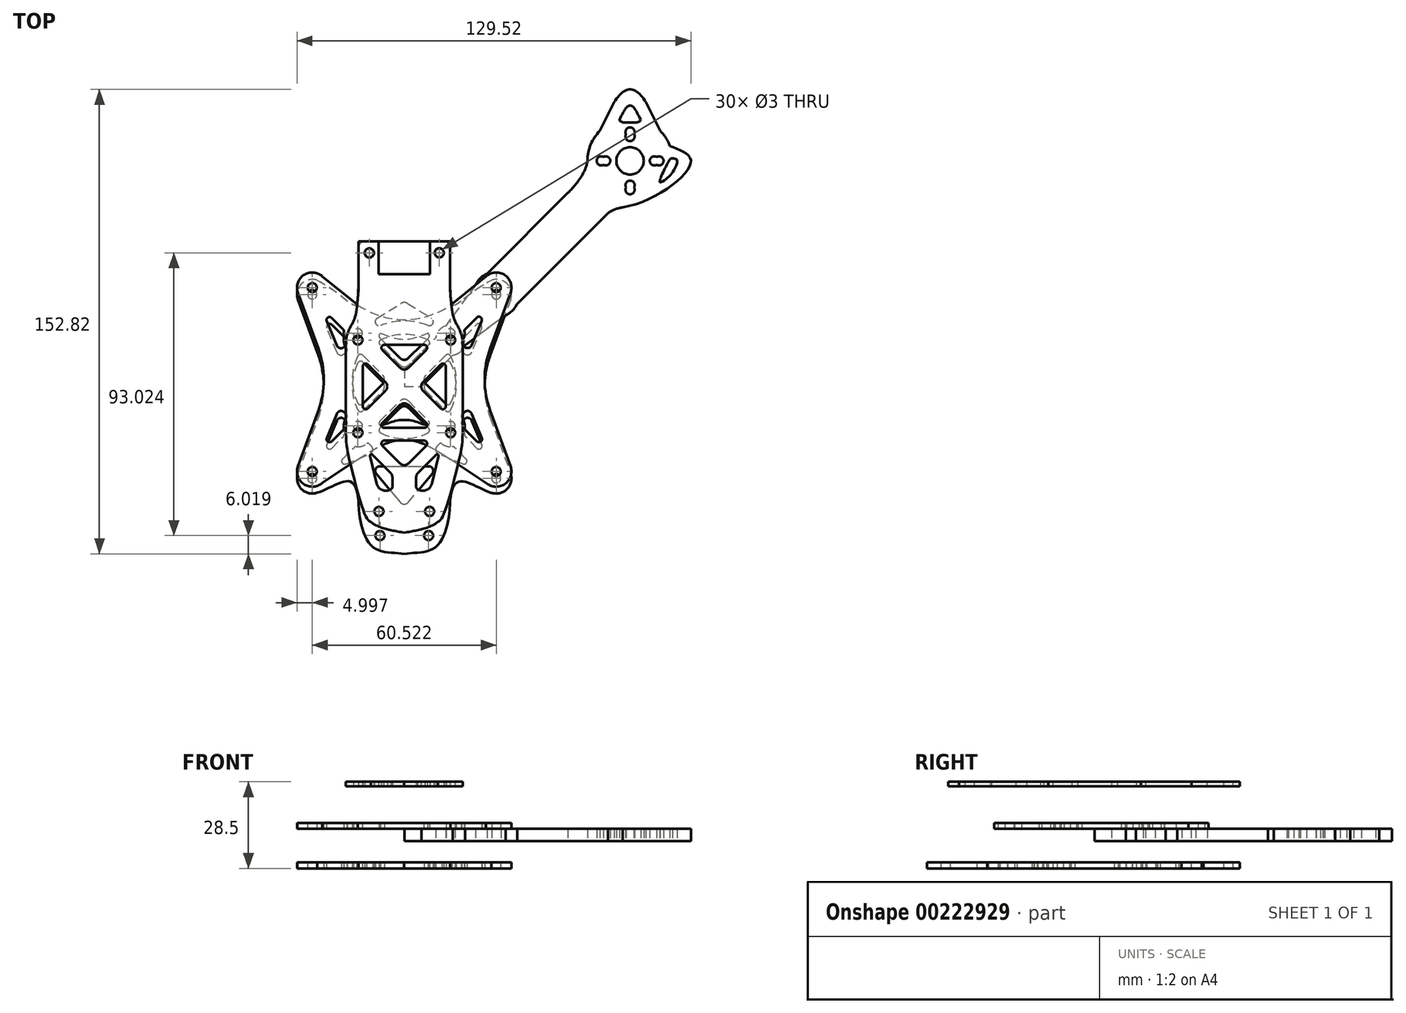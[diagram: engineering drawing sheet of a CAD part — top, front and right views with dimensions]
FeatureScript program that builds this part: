
annotation { "Feature Type Name" : "Feature", "Feature Type Description" : "" }
export const myFeature = defineFeature(function(context is Context, id is Id, definition is map)
    precondition{}
    {
        {
            var Q0;
            Q0=qCreatedBy(makeId("Top.planeOp"),FACE);
            var sketch = newSketch(context, id + "F0", { "sketchPlane" : qUnion([Q0])});
            skLineSegment(sketch, "E0.bottom", {"start": v(-15.25, 15.25) * mm, "end": v(15.25, 15.25) * mm, "construction": true});
            skLineSegment(sketch, "E0.top", {"start": v(-15.25, -15.25) * mm, "end": v(15.25, -15.25) * mm, "construction": true});
            skLineSegment(sketch, "E0.left", {"start": v(-15.25, 15.25) * mm, "end": v(-15.25, -15.25) * mm, "construction": true});
            skLineSegment(sketch, "E0.right", {"start": v(15.25, 15.25) * mm, "end": v(15.25, -15.25) * mm, "construction": true});
            skPoint(sketch, "E0.middle", {"position": v(0, 0) * mm});
            skLineSegment(sketch, "E1.bottom", {"start": v(30.25, 30.25) * mm, "end": v(-30.25, 30.25) * mm, "construction": true});
            skLineSegment(sketch, "E1.top", {"start": v(30.25, -30.25) * mm, "end": v(-30.25, -30.25) * mm, "construction": true});
            skLineSegment(sketch, "E1.left", {"start": v(30.25, 30.25) * mm, "end": v(30.25, -30.25) * mm, "construction": true});
            skLineSegment(sketch, "E1.right", {"start": v(-30.25, 30.25) * mm, "end": v(-30.25, -30.25) * mm, "construction": true});
            skLineSegment(sketch, "E2.bottom", {"start": v(-74.25, 74.24) * mm, "end": v(74.25, 74.24) * mm, "construction": true});
            skLineSegment(sketch, "E2.top", {"start": v(-74.25, -74.25) * mm, "end": v(74.24, -74.25) * mm, "construction": true});
            skLineSegment(sketch, "E2.left", {"start": v(-74.25, 74.24) * mm, "end": v(-74.25, -74.25) * mm, "construction": true});
            skLineSegment(sketch, "E2.right", {"start": v(74.24, 74.24) * mm, "end": v(74.24, -74.25) * mm, "construction": true});
            skCircle(sketch, "E3", {"center": v(74.25, 74.24) * mm, "radius": 8 * mm, "construction": true});
            skCircle(sketch, "E4", {"center": v(74.24, -74.25) * mm, "radius": 8 * mm, "construction": true});
            skCircle(sketch, "E5", {"center": v(-74.25, -74.25) * mm, "radius": 8 * mm, "construction": true});
            skCircle(sketch, "E6", {"center": v(-74.25, 74.24) * mm, "radius": 8 * mm, "construction": true});
            skCircle(sketch, "E7", {"center": v(74.25, 74.24) * mm, "radius": 9.5 * mm, "construction": true});
            skCircle(sketch, "E8", {"center": v(74.24, -74.25) * mm, "radius": 9.5 * mm, "construction": true});
            skCircle(sketch, "E9", {"center": v(-74.25, -74.25) * mm, "radius": 9.5 * mm, "construction": true});
            skCircle(sketch, "E10", {"center": v(-74.25, 74.24) * mm, "radius": 9.5 * mm, "construction": true});
            skCircle(sketch, "E11", {"center": v(74.25, 74.24) * mm, "radius": 14 * mm, "construction": true});
            skCircle(sketch, "E12", {"center": v(-74.25, 74.24) * mm, "radius": 14 * mm, "construction": true});
            skCircle(sketch, "E13", {"center": v(74.24, -74.25) * mm, "radius": 14 * mm, "construction": true});
            skCircle(sketch, "E14", {"center": v(-74.25, -74.25) * mm, "radius": 14 * mm, "construction": true});
            skCircle(sketch, "E15", {"center": v(74.25, 74.24) * mm, "radius": 63.5 * mm, "construction": true});
            skCircle(sketch, "E16", {"center": v(74.24, -74.25) * mm, "radius": 63.5 * mm, "construction": true});
            skCircle(sketch, "E17", {"center": v(-74.25, -74.25) * mm, "radius": 63.5 * mm, "construction": true});
            skCircle(sketch, "E18", {"center": v(-74.25, 74.24) * mm, "radius": 63.5 * mm, "construction": true});
            skLineSegment(sketch, "E19", {"start": v(0, 30.25) * mm, "end": v(0, 37.76) * mm, "construction": true});
            skLineSegment(sketch, "E20", {"start": v(0, 37.76) * mm, "end": v(-15, 37.76) * mm, "construction": true});
            skLineSegment(sketch, "E21", {"start": v(0, 37.76) * mm, "end": v(15, 37.76) * mm, "construction": true});
            skLineSegment(sketch, "E22", {"start": v(0, -30.25) * mm, "end": v(0, -37.76) * mm, "construction": true});
            skLineSegment(sketch, "E23.bottom", {"start": v(-26.17, 26.25) * mm, "end": v(26.21, 26.25) * mm, "construction": true});
            skLineSegment(sketch, "E23.top", {"start": v(-26.21, -26.25) * mm, "end": v(26.17, -26.25) * mm, "construction": true});
            skLineSegment(sketch, "E23.left", {"start": v(-26.17, 26.25) * mm, "end": v(-26.17, -26.13) * mm, "construction": true});
            skLineSegment(sketch, "E23.right", {"start": v(26.21, 26.25) * mm, "end": v(26.21, -26.2) * mm, "construction": true});
            skCircle(sketch, "E24", {"center": v(30.25, 30.25) * mm, "radius": 5 * mm, "construction": true});
            skCircle(sketch, "E25", {"center": v(-30.25, 30.25) * mm, "radius": 5 * mm, "construction": true});
            skCircle(sketch, "E26", {"center": v(30.25, -30.25) * mm, "radius": 5 * mm, "construction": true});
            skCircle(sketch, "E27", {"center": v(-30.25, -30.25) * mm, "radius": 5 * mm, "construction": true});
            skLineSegment(sketch, "E28.bottom", {"start": v(24.5, 24.5) * mm, "end": v(-24.5, 24.5) * mm, "construction": true});
            skLineSegment(sketch, "E28.top", {"start": v(24.5, -24.5) * mm, "end": v(-24.5, -24.5) * mm, "construction": true});
            skLineSegment(sketch, "E28.left", {"start": v(24.5, 24.5) * mm, "end": v(24.5, -24.5) * mm, "construction": true});
            skLineSegment(sketch, "E28.right", {"start": v(-24.5, 24.5) * mm, "end": v(-24.5, -24.5) * mm, "construction": true});
            skLineSegment(sketch, "E29", {"start": v(-26.17, 26.25) * mm, "end": v(-30.25, 30.25) * mm, "construction": true});
            skLineSegment(sketch, "E30", {"start": v(-26.68, 26.75) * mm, "end": v(-33.82, 33.75) * mm, "construction": true});
            skLineSegment(sketch, "E31", {"start": v(-31.8, 31.77) * mm, "end": v(-28.66, 34.99) * mm, "construction": true});
            skLineSegment(sketch, "E32", {"start": v(-31.8, 31.77) * mm, "end": v(-34.96, 28.56) * mm, "construction": true});
            skArc(sketch, "E33", {"start": v(-28.66, 34.99) * mm, "mid": v(-33.82, 33.75) * mm, "end": v(-34.96, 28.56) * mm});
            skLineSegment(sketch, "E34", {"start": v(26.21, 26.25) * mm, "end": v(30.25, 30.25) * mm, "construction": true});
            skLineSegment(sketch, "E35", {"start": v(26.7, 26.73) * mm, "end": v(33.8, 33.77) * mm, "construction": true});
            skLineSegment(sketch, "E36", {"start": v(31.8, 31.78) * mm, "end": v(34.96, 28.58) * mm, "construction": true});
            skLineSegment(sketch, "E37", {"start": v(31.8, 31.78) * mm, "end": v(28.63, 34.98) * mm, "construction": true});
            skArc(sketch, "E38", {"start": v(34.96, 28.58) * mm, "mid": v(33.8, 33.77) * mm, "end": v(28.63, 34.98) * mm});
            skLineSegment(sketch, "E39", {"start": v(26.17, -26.25) * mm, "end": v(30.25, -30.25) * mm, "construction": true});
            skLineSegment(sketch, "E40", {"start": v(26.68, -26.75) * mm, "end": v(33.82, -33.75) * mm, "construction": true});
            skLineSegment(sketch, "E41", {"start": v(31.8, -31.78) * mm, "end": v(34.96, -28.56) * mm, "construction": true});
            skLineSegment(sketch, "E42", {"start": v(31.8, -31.78) * mm, "end": v(28.66, -35) * mm, "construction": true});
            skArc(sketch, "E43", {"start": v(28.66, -35) * mm, "mid": v(33.82, -33.75) * mm, "end": v(34.96, -28.56) * mm});
            skLineSegment(sketch, "E44", {"start": v(-26.21, -26.25) * mm, "end": v(-30.25, -30.25) * mm, "construction": true});
            skLineSegment(sketch, "E45", {"start": v(-26.7, -26.73) * mm, "end": v(-33.8, -33.77) * mm, "construction": true});
            skLineSegment(sketch, "E46", {"start": v(-31.8, -31.78) * mm, "end": v(-28.63, -34.98) * mm, "construction": true});
            skLineSegment(sketch, "E47", {"start": v(-31.8, -31.78) * mm, "end": v(-34.96, -28.58) * mm, "construction": true});
            skArc(sketch, "E48", {"start": v(-34.96, -28.58) * mm, "mid": v(-33.8, -33.77) * mm, "end": v(-28.63, -34.98) * mm});
            skLineSegment(sketch, "E49", {"start": v(-34.96, -28.58) * mm, "end": v(-28.28, -10.31) * mm});
            skLineSegment(sketch, "E50", {"start": v(-28.28, 10.31) * mm, "end": v(-34.96, 28.56) * mm});
            skLineSegment(sketch, "E51", {"start": v(34.96, 28.58) * mm, "end": v(28.28, 10.31) * mm});
            skLineSegment(sketch, "E52", {"start": v(28.28, -10.31) * mm, "end": v(34.96, -28.56) * mm});
            skPoint(sketch, "E53.visualSharp", {"position": v(24.5, 0) * mm});
            skArc(sketch, "E53.filletArc", {"start": v(28.28, 10.31) * mm, "mid": v(26.45, 0) * mm, "end": v(28.28, -10.31) * mm});
            skPoint(sketch, "E54.visualSharp", {"position": v(-24.5, 0) * mm});
            skArc(sketch, "E54.filletArc", {"start": v(-28.28, -10.31) * mm, "mid": v(-26.45, 0) * mm, "end": v(-28.28, 10.31) * mm});
            skFitSpline(sketch, "E55", {"points": [v(-28.66, 34.99) * mm, v(-15, 37.76) * mm], "startDerivative": vector(40.9, -21.49) * mm, "endDerivative": vector(0.75, 54.16) * mm});
            skFitSpline(sketch, "E56", {"points": [v(15, 37.76) * mm, v(28.63, 34.98) * mm], "startDerivative": vector(0.75, -54.16) * mm, "endDerivative": vector(40.9, 21.46) * mm});
            skLineSegment(sketch, "E57", {"start": v(-15.25, 19.7) * mm, "end": v(15.25, 19.7) * mm, "construction": true});
            skPoint(sketch, "E58.endSnap0", {"position": v(0, -15.25) * mm});
            skLineSegment(sketch, "E59", {"start": v(-15.25, -19.7) * mm, "end": v(15.25, -19.7) * mm, "construction": true});
            skCircle(sketch, "E60", {"center": v(-30.25, 30.25) * mm, "radius": 1.5 * mm});
            skCircle(sketch, "E61", {"center": v(30.25, 30.25) * mm, "radius": 1.5 * mm});
            skCircle(sketch, "E62", {"center": v(15.25, 15.25) * mm, "radius": 1.5 * mm});
            skCircle(sketch, "E63", {"center": v(-15.25, 15.25) * mm, "radius": 1.5 * mm});
            skCircle(sketch, "E64", {"center": v(-15.25, -15.25) * mm, "radius": 1.5 * mm});
            skCircle(sketch, "E65", {"center": v(15.25, -15.25) * mm, "radius": 1.5 * mm});
            skCircle(sketch, "E66", {"center": v(30.25, -30.25) * mm, "radius": 1.5 * mm});
            skCircle(sketch, "E67", {"center": v(-30.25, -30.25) * mm, "radius": 1.5 * mm});
            skLineSegment(sketch, "E68", {"start": v(15, 37.76) * mm, "end": v(11.5, 37.76) * mm, "construction": true});
            skLineSegment(sketch, "E69", {"start": v(-15, 37.76) * mm, "end": v(-11.5, 37.76) * mm, "construction": true});
            skCircle(sketch, "E70", {"center": v(-11.5, 43.96) * mm, "radius": 1.5 * mm});
            skCircle(sketch, "E71", {"center": v(11.5, 43.96) * mm, "radius": 1.5 * mm});
            skLineSegment(sketch, "E72", {"start": v(0, 37.76) * mm, "end": v(0, 15.25) * mm, "construction": true});
            skLineSegment(sketch, "E73", {"start": v(0, -52.26) * mm, "end": v(-11, -52.26) * mm, "construction": true});
            skLineSegment(sketch, "E74", {"start": v(0, -52.26) * mm, "end": v(11, -52.26) * mm, "construction": true});
            skPoint(sketch, "E75.visualSharp", {"position": v(-15, -39.16) * mm});
            skPoint(sketch, "E76.visualSharp", {"position": v(15, -39.15) * mm});
            skCircle(sketch, "E77", {"center": v(0, 0) * mm, "radius": 17.11 * mm, "construction": true});
            skLineSegment(sketch, "E78", {"start": v(0, 0) * mm, "end": v(14.1, 14.1) * mm, "construction": true});
            skLineSegment(sketch, "E79", {"start": v(0, 0) * mm, "end": v(-15.25, 15.25) * mm, "construction": true});
            skLineSegment(sketch, "E80", {"start": v(0, 0) * mm, "end": v(-15.32, -15.32) * mm, "construction": true});
            skLineSegment(sketch, "E81", {"start": v(0, 0) * mm, "end": v(15.25, -15.25) * mm, "construction": true});
            skLineSegment(sketch, "E82", {"start": v(-10.7, 10.7) * mm, "end": v(-7.86, 13.52) * mm, "construction": true});
            skLineSegment(sketch, "E83", {"start": v(-10.7, 10.7) * mm, "end": v(-13.52, 7.86) * mm, "construction": true});
            skLineSegment(sketch, "E84", {"start": v(9.03, 9.03) * mm, "end": v(11.86, 6.2) * mm, "construction": true});
            skLineSegment(sketch, "E85", {"start": v(9.03, 9.03) * mm, "end": v(6.2, 11.86) * mm, "construction": true});
            skLineSegment(sketch, "E86", {"start": v(9.8, -9.8) * mm, "end": v(12.64, -6.98) * mm, "construction": true});
            skLineSegment(sketch, "E87", {"start": v(9.8, -9.8) * mm, "end": v(6.98, -12.64) * mm, "construction": true});
            skLineSegment(sketch, "E88", {"start": v(-9.52, -9.52) * mm, "end": v(-6.7, -12.35) * mm, "construction": true});
            skLineSegment(sketch, "E89", {"start": v(-9.52, -9.52) * mm, "end": v(-12.35, -6.7) * mm, "construction": true});
            skLineSegment(sketch, "E90.bottom", {"start": v(6.35, 6.35) * mm, "end": v(-6.35, 6.35) * mm, "construction": true});
            skLineSegment(sketch, "E90.top", {"start": v(6.35, -6.35) * mm, "end": v(-6.35, -6.35) * mm, "construction": true});
            skLineSegment(sketch, "E90.left", {"start": v(6.35, 6.35) * mm, "end": v(6.35, -6.35) * mm, "construction": true});
            skLineSegment(sketch, "E90.right", {"start": v(-6.35, 6.35) * mm, "end": v(-6.35, -6.35) * mm, "construction": true});
            skLineSegment(sketch, "E91", {"start": v(6.2, 11.86) * mm, "end": v(8.94, 14.6) * mm, "construction": true});
            skLineSegment(sketch, "E92", {"start": v(11.86, 6.2) * mm, "end": v(14.6, 8.94) * mm, "construction": true});
            skLineSegment(sketch, "E93", {"start": v(8, 13.66) * mm, "end": v(1.41, 7.07) * mm});
            skLineSegment(sketch, "E94", {"start": v(-1.41, 7.07) * mm, "end": v(-8, 13.66) * mm});
            skLineSegment(sketch, "E95", {"start": v(-13.52, 7.86) * mm, "end": v(-14.6, 8.94) * mm, "construction": true});
            skLineSegment(sketch, "E96", {"start": v(-6.7, -12.35) * mm, "end": v(-8.94, -14.6) * mm, "construction": true});
            skLineSegment(sketch, "E97", {"start": v(-8, -13.66) * mm, "end": v(-1.41, -7.07) * mm});
            skLineSegment(sketch, "E98", {"start": v(1.41, -7.07) * mm, "end": v(8, -13.66) * mm});
            skLineSegment(sketch, "E99", {"start": v(13.66, 8) * mm, "end": v(7.07, 1.41) * mm});
            skLineSegment(sketch, "E100", {"start": v(7.07, -1.41) * mm, "end": v(13.66, -8) * mm});
            skPoint(sketch, "E101", {"position": v(-7.77, 15.25) * mm});
            skPoint(sketch, "E102", {"position": v(7.77, 15.25) * mm});
            skPoint(sketch, "E103", {"position": v(15.25, 7.77) * mm});
            skPoint(sketch, "E104", {"position": v(15.25, -7.77) * mm});
            skPoint(sketch, "E105", {"position": v(7.77, -15.25) * mm});
            skPoint(sketch, "E106", {"position": v(-7.77, -15.25) * mm});
            skPoint(sketch, "E107", {"position": v(-15.25, -7.77) * mm});
            skPoint(sketch, "E108", {"position": v(-15.25, 7.77) * mm});
            skLineSegment(sketch, "E109", {"start": v(-7.79, 15.24) * mm, "end": v(-7.77, 15.25) * mm});
            skLineSegment(sketch, "E110", {"start": v(7.79, 15.24) * mm, "end": v(7.77, 15.25) * mm});
            skLineSegment(sketch, "E111", {"start": v(15.24, 7.79) * mm, "end": v(15.25, 7.77) * mm});
            skLineSegment(sketch, "E112", {"start": v(15.24, -7.79) * mm, "end": v(15.25, -7.77) * mm});
            skLineSegment(sketch, "E113", {"start": v(7.79, -15.24) * mm, "end": v(7.77, -15.25) * mm});
            skLineSegment(sketch, "E114", {"start": v(-7.77, -15.25) * mm, "end": v(-7.79, -15.24) * mm});
            skLineSegment(sketch, "E115", {"start": v(-15.24, -7.79) * mm, "end": v(-15.25, -7.77) * mm});
            skLineSegment(sketch, "E116", {"start": v(-15.24, 7.79) * mm, "end": v(-15.25, 7.77) * mm});
            skPoint(sketch, "E117", {"position": v(0, 17.11) * mm});
            skPoint(sketch, "E118", {"position": v(17.11, 0) * mm});
            skPoint(sketch, "E119", {"position": v(-17.11, 0) * mm});
            skPoint(sketch, "E120", {"position": v(0, -17.11) * mm});
            skArc(sketch, "E121", {"start": v(7.77, 15.25) * mm, "mid": v(0, 17.11) * mm, "end": v(-7.77, 15.25) * mm});
            skArc(sketch, "E122", {"start": v(15.25, -7.77) * mm, "mid": v(17.11, 0) * mm, "end": v(15.25, 7.77) * mm});
            skArc(sketch, "E123", {"start": v(-7.77, -15.25) * mm, "mid": v(0, -17.11) * mm, "end": v(7.77, -15.25) * mm});
            skArc(sketch, "E124", {"start": v(-15.25, 7.77) * mm, "mid": v(-17.11, 0) * mm, "end": v(-15.25, -7.77) * mm});
            skPoint(sketch, "E125.visualSharp", {"position": v(-5.66, 0) * mm});
            skPoint(sketch, "E126.visualSharp", {"position": v(-14.6, 8.94) * mm});
            skArc(sketch, "E126.filletArc", {"start": v(-13.66, 8) * mm, "mid": v(-14.5, 8.29) * mm, "end": v(-15.24, 7.79) * mm});
            skPoint(sketch, "E127.visualSharp", {"position": v(-14.55, -9.02) * mm});
            skArc(sketch, "E127.filletArc", {"start": v(-15.24, -7.79) * mm, "mid": v(-14.5, -8.29) * mm, "end": v(-13.66, -8) * mm});
            skPoint(sketch, "E128.visualSharp", {"position": v(-8.94, 14.6) * mm});
            skArc(sketch, "E128.filletArc", {"start": v(-7.79, 15.24) * mm, "mid": v(-8.29, 14.5) * mm, "end": v(-8, 13.66) * mm});
            skPoint(sketch, "E129.visualSharp", {"position": v(8.94, 14.6) * mm});
            skArc(sketch, "E129.filletArc", {"start": v(8, 13.66) * mm, "mid": v(8.29, 14.5) * mm, "end": v(7.79, 15.24) * mm});
            skPoint(sketch, "E130.visualSharp", {"position": v(14.6, -8.94) * mm});
            skArc(sketch, "E130.filletArc", {"start": v(13.66, -8) * mm, "mid": v(14.5, -8.29) * mm, "end": v(15.24, -7.79) * mm});
            skPoint(sketch, "E131.visualSharp", {"position": v(14.6, 8.94) * mm});
            skArc(sketch, "E131.filletArc", {"start": v(15.24, 7.79) * mm, "mid": v(14.5, 8.29) * mm, "end": v(13.66, 8) * mm});
            skPoint(sketch, "E132.visualSharp", {"position": v(8.94, -14.6) * mm});
            skArc(sketch, "E132.filletArc", {"start": v(7.79, -15.24) * mm, "mid": v(8.29, -14.5) * mm, "end": v(8, -13.66) * mm});
            skPoint(sketch, "E133.visualSharp", {"position": v(-8.94, -14.6) * mm});
            skArc(sketch, "E133.filletArc", {"start": v(-8, -13.66) * mm, "mid": v(-8.29, -14.5) * mm, "end": v(-7.79, -15.24) * mm});
            skLineSegment(sketch, "E134", {"start": v(-13.66, 8) * mm, "end": v(-7.07, 1.41) * mm});
            skLineSegment(sketch, "E135", {"start": v(-13.66, -8) * mm, "end": v(-7.07, -1.41) * mm});
            skArc(sketch, "E136.filletArc", {"start": v(-7.07, -1.41) * mm, "mid": v(-6.49, 0) * mm, "end": v(-7.07, 1.41) * mm});
            skPoint(sketch, "E137.visualSharp", {"position": v(0, -5.66) * mm});
            skArc(sketch, "E137.filletArc", {"start": v(1.41, -7.07) * mm, "mid": v(0, -6.49) * mm, "end": v(-1.41, -7.07) * mm});
            skPoint(sketch, "E138.visualSharp", {"position": v(5.66, 0) * mm});
            skArc(sketch, "E138.filletArc", {"start": v(7.07, 1.41) * mm, "mid": v(6.49, 0) * mm, "end": v(7.07, -1.41) * mm});
            skPoint(sketch, "E139.visualSharp", {"position": v(0, 5.66) * mm});
            skArc(sketch, "E139.filletArc", {"start": v(-1.41, 7.07) * mm, "mid": v(0, 6.49) * mm, "end": v(1.41, 7.07) * mm});
            skLineSegment(sketch, "E140", {"start": v(-12.9, 12.9) * mm, "end": v(-11.14, 14.67) * mm, "construction": true});
            skLineSegment(sketch, "E141", {"start": v(-12.9, 12.9) * mm, "end": v(-14.67, 11.14) * mm, "construction": true});
            skLineSegment(sketch, "E142", {"start": v(-14.67, 11.14) * mm, "end": v(-27.4, 23.87) * mm, "construction": true});
            skPoint(sketch, "E143", {"position": v(-17.57, 14.03) * mm});
            skCircle(sketch, "E144", {"center": v(-15.25, 15.25) * mm, "radius": 4.62 * mm, "construction": true});
            skLineSegment(sketch, "E145", {"start": v(-27.4, 23.87) * mm, "end": v(-21.1, 8.64) * mm, "construction": true});
            skLineSegment(sketch, "E146", {"start": v(-15.25, 15.25) * mm, "end": v(-21.32, 9.18) * mm, "construction": true});
            skLineSegment(sketch, "E147", {"start": v(-18.86, 11.64) * mm, "end": v(-19.74, 10.76) * mm});
            skLineSegment(sketch, "E148", {"start": v(-22.18, 11.25) * mm, "end": v(-25.48, 19.23) * mm});
            skLineSegment(sketch, "E149", {"start": v(-23.85, 20.32) * mm, "end": v(-20.04, 16.5) * mm});
            skLineSegment(sketch, "E150", {"start": v(-19.83, 15.85) * mm, "end": v(-19.85, 15.74) * mm});
            skLineSegment(sketch, "E151", {"start": v(-18.84, 12.33) * mm, "end": v(-18.85, 12.35) * mm});
            skPoint(sketch, "E152", {"position": v(-19.67, 13.9) * mm});
            skArc(sketch, "E153", {"start": v(-19.85, 15.74) * mm, "mid": v(-19.69, 13.95) * mm, "end": v(-18.85, 12.35) * mm});
            skPoint(sketch, "E154.visualSharp", {"position": v(-27.4, 23.87) * mm});
            skArc(sketch, "E154.filletArc", {"start": v(-23.85, 20.32) * mm, "mid": v(-25.11, 20.44) * mm, "end": v(-25.48, 19.23) * mm});
            skPoint(sketch, "E155.visualSharp", {"position": v(-21.32, 9.18) * mm});
            skArc(sketch, "E155.filletArc", {"start": v(-22.18, 11.25) * mm, "mid": v(-21.1, 10.35) * mm, "end": v(-19.74, 10.76) * mm});
            skPoint(sketch, "E156.visualSharp", {"position": v(-18.52, 11.98) * mm});
            skArc(sketch, "E156.filletArc", {"start": v(-18.86, 11.64) * mm, "mid": v(-18.7, 11.98) * mm, "end": v(-18.84, 12.33) * mm});
            skPoint(sketch, "E157.visualSharp", {"position": v(-19.77, 16.23) * mm});
            skArc(sketch, "E157.filletArc", {"start": v(-19.83, 15.85) * mm, "mid": v(-19.86, 16.2) * mm, "end": v(-20.04, 16.5) * mm});
            skCircle(sketch, "E158", {"center": v(15.23, 15.26) * mm, "radius": 4.62 * mm, "construction": true});
            skLineSegment(sketch, "E159", {"start": v(15.23, 15.26) * mm, "end": v(12.9, 12.9) * mm, "construction": true});
            skLineSegment(sketch, "E160", {"start": v(12.9, 12.9) * mm, "end": v(14.68, 11.15) * mm, "construction": true});
            skLineSegment(sketch, "E161", {"start": v(12.9, 12.9) * mm, "end": v(11.12, 14.66) * mm, "construction": true});
            skLineSegment(sketch, "E162", {"start": v(11.12, 14.66) * mm, "end": v(23.85, 27.39) * mm, "construction": true});
            skLineSegment(sketch, "E163", {"start": v(14.68, 11.15) * mm, "end": v(27.32, 23.97) * mm, "construction": true});
            skLineSegment(sketch, "E164", {"start": v(15.25, 15.25) * mm, "end": v(21.37, 9.22) * mm, "construction": true});
            skLineSegment(sketch, "E165", {"start": v(21.37, 9.22) * mm, "end": v(27.32, 23.97) * mm, "construction": true});
            skLineSegment(sketch, "E166", {"start": v(19.8, 15.9) * mm, "end": v(19.82, 15.79) * mm});
            skLineSegment(sketch, "E167", {"start": v(18.84, 12.37) * mm, "end": v(18.86, 12.4) * mm});
            skLineSegment(sketch, "E168", {"start": v(20.01, 16.55) * mm, "end": v(23.8, 20.4) * mm});
            skLineSegment(sketch, "E169", {"start": v(25.45, 19.33) * mm, "end": v(22.2, 11.3) * mm});
            skLineSegment(sketch, "E170", {"start": v(19.77, 10.8) * mm, "end": v(18.86, 11.69) * mm});
            skPoint(sketch, "E171", {"position": v(19.65, 13.92) * mm});
            skArc(sketch, "E172", {"start": v(18.86, 12.4) * mm, "mid": v(19.68, 14) * mm, "end": v(19.82, 15.79) * mm});
            skPoint(sketch, "E173.visualSharp", {"position": v(18.53, 12.02) * mm});
            skArc(sketch, "E173.filletArc", {"start": v(18.84, 12.37) * mm, "mid": v(18.72, 12.03) * mm, "end": v(18.86, 11.69) * mm});
            skPoint(sketch, "E174.visualSharp", {"position": v(19.74, 16.28) * mm});
            skArc(sketch, "E174.filletArc", {"start": v(20.01, 16.55) * mm, "mid": v(19.83, 16.25) * mm, "end": v(19.8, 15.9) * mm});
            skPoint(sketch, "E175.visualSharp", {"position": v(27.32, 23.97) * mm});
            skArc(sketch, "E175.filletArc", {"start": v(25.45, 19.33) * mm, "mid": v(25.07, 20.54) * mm, "end": v(23.8, 20.4) * mm});
            skPoint(sketch, "E176.visualSharp", {"position": v(21.37, 9.22) * mm});
            skArc(sketch, "E176.filletArc", {"start": v(19.77, 10.8) * mm, "mid": v(21.12, 10.4) * mm, "end": v(22.2, 11.3) * mm});
            skCircle(sketch, "E177", {"center": v(-15.25, -15.25) * mm, "radius": 4.62 * mm, "construction": true});
            skCircle(sketch, "E178", {"center": v(15.25, -15.25) * mm, "radius": 4.62 * mm, "construction": true});
            skLineSegment(sketch, "E179", {"start": v(-15.25, -15.25) * mm, "end": v(-12.9, -12.9) * mm, "construction": true});
            skLineSegment(sketch, "E180", {"start": v(-12.9, -12.9) * mm, "end": v(-11.14, -14.67) * mm, "construction": true});
            skLineSegment(sketch, "E181", {"start": v(-12.9, -12.9) * mm, "end": v(-14.67, -11.14) * mm, "construction": true});
            skLineSegment(sketch, "E182", {"start": v(-11.14, -14.67) * mm, "end": v(-23.87, -27.4) * mm, "construction": true});
            skLineSegment(sketch, "E183", {"start": v(-14.67, -11.14) * mm, "end": v(-27.4, -23.87) * mm, "construction": true});
            skLineSegment(sketch, "E184", {"start": v(-15.25, -15.25) * mm, "end": v(-9.18, -21.32) * mm, "construction": true});
            skLineSegment(sketch, "E185", {"start": v(-15.25, -15.25) * mm, "end": v(-21.32, -9.18) * mm, "construction": true});
            skLineSegment(sketch, "E186", {"start": v(-25.48, -19.23) * mm, "end": v(-22.18, -11.25) * mm});
            skLineSegment(sketch, "E187", {"start": v(-19.74, -10.76) * mm, "end": v(-18.86, -11.64) * mm});
            skLineSegment(sketch, "E188", {"start": v(-23.85, -20.32) * mm, "end": v(-20.04, -16.5) * mm});
            skLineSegment(sketch, "E189", {"start": v(-18.84, -12.33) * mm, "end": v(-18.85, -12.35) * mm});
            skLineSegment(sketch, "E190", {"start": v(-19.83, -15.86) * mm, "end": v(-19.85, -15.74) * mm});
            skPoint(sketch, "E191", {"position": v(-19.69, -13.94) * mm});
            skArc(sketch, "E192", {"start": v(-18.85, -12.35) * mm, "mid": v(-19.69, -13.95) * mm, "end": v(-19.85, -15.74) * mm});
            skPoint(sketch, "E193.visualSharp", {"position": v(-18.52, -11.98) * mm});
            skArc(sketch, "E193.filletArc", {"start": v(-18.84, -12.33) * mm, "mid": v(-18.7, -11.98) * mm, "end": v(-18.86, -11.64) * mm});
            skPoint(sketch, "E194.visualSharp", {"position": v(-19.77, -16.23) * mm});
            skArc(sketch, "E194.filletArc", {"start": v(-20.04, -16.5) * mm, "mid": v(-19.86, -16.2) * mm, "end": v(-19.83, -15.86) * mm});
            skPoint(sketch, "E195.visualSharp", {"position": v(-27.4, -23.87) * mm});
            skArc(sketch, "E195.filletArc", {"start": v(-25.48, -19.23) * mm, "mid": v(-25.11, -20.44) * mm, "end": v(-23.85, -20.32) * mm});
            skPoint(sketch, "E196.visualSharp", {"position": v(-21.32, -9.18) * mm});
            skArc(sketch, "E196.filletArc", {"start": v(-19.74, -10.76) * mm, "mid": v(-21.1, -10.35) * mm, "end": v(-22.18, -11.25) * mm});
            skLineSegment(sketch, "E197", {"start": v(15.25, -15.25) * mm, "end": v(12.9, -12.9) * mm, "construction": true});
            skLineSegment(sketch, "E198", {"start": v(12.9, -12.9) * mm, "end": v(14.67, -11.14) * mm, "construction": true});
            skLineSegment(sketch, "E199", {"start": v(12.9, -12.9) * mm, "end": v(11.14, -14.67) * mm, "construction": true});
            skLineSegment(sketch, "E200", {"start": v(14.67, -11.14) * mm, "end": v(27.4, -23.87) * mm, "construction": true});
            skLineSegment(sketch, "E201", {"start": v(15.25, -15.25) * mm, "end": v(21.32, -9.18) * mm, "construction": true});
            skLineSegment(sketch, "E202", {"start": v(22.18, -11.25) * mm, "end": v(25.48, -19.23) * mm});
            skLineSegment(sketch, "E203", {"start": v(23.85, -20.32) * mm, "end": v(20.04, -16.5) * mm});
            skLineSegment(sketch, "E204", {"start": v(19.74, -10.76) * mm, "end": v(18.86, -11.64) * mm});
            skLineSegment(sketch, "E205", {"start": v(18.84, -12.33) * mm, "end": v(18.85, -12.35) * mm});
            skLineSegment(sketch, "E206", {"start": v(19.83, -15.86) * mm, "end": v(19.85, -15.74) * mm});
            skPoint(sketch, "E207", {"position": v(19.64, -13.8) * mm});
            skArc(sketch, "E208", {"start": v(19.85, -15.74) * mm, "mid": v(19.69, -13.95) * mm, "end": v(18.85, -12.35) * mm});
            skPoint(sketch, "E209.visualSharp", {"position": v(21.32, -9.18) * mm});
            skArc(sketch, "E209.filletArc", {"start": v(22.18, -11.25) * mm, "mid": v(21.1, -10.35) * mm, "end": v(19.74, -10.76) * mm});
            skPoint(sketch, "E210.visualSharp", {"position": v(19.77, -16.23) * mm});
            skArc(sketch, "E210.filletArc", {"start": v(19.83, -15.86) * mm, "mid": v(19.86, -16.2) * mm, "end": v(20.04, -16.5) * mm});
            skPoint(sketch, "E211.visualSharp", {"position": v(18.52, -11.98) * mm});
            skArc(sketch, "E211.filletArc", {"start": v(18.86, -11.64) * mm, "mid": v(18.7, -11.98) * mm, "end": v(18.84, -12.33) * mm});
            skPoint(sketch, "E212.visualSharp", {"position": v(27.4, -23.87) * mm});
            skArc(sketch, "E212.filletArc", {"start": v(23.85, -20.32) * mm, "mid": v(25.11, -20.44) * mm, "end": v(25.48, -19.23) * mm});
            skPoint(sketch, "E213", {"position": v(0, -55.07) * mm});
            skLineSegment(sketch, "E214", {"start": v(0, -31.44) * mm, "end": v(17.54, -31.44) * mm, "construction": true});
            skLineSegment(sketch, "E215", {"start": v(0.01, -31.43) * mm, "end": v(-17.53, -31.43) * mm, "construction": true});
            skFitSpline(sketch, "E216", {"points": [v(28.66, -35) * mm, v(17.54, -31.44) * mm, v(15, -39.15) * mm], "startDerivative": vector(-22.15, 6.9) * mm, "endDerivative": vector(0, -15.3) * mm});
            skFitSpline(sketch, "E217", {"points": [v(15, -39.15) * mm, v(11, -52.26) * mm, v(0, -55.07) * mm], "startDerivative": vector(0, -14.3) * mm, "endDerivative": vector(-23.36, -3.95) * mm});
            skFitSpline(sketch, "E218", {"points": [v(-28.63, -34.98) * mm, v(-17.53, -31.43) * mm, v(-15, -39.16) * mm], "startDerivative": vector(22.11, 6.89) * mm, "endDerivative": vector(0, -15.33) * mm});
            skFitSpline(sketch, "E219", {"points": [v(-15, -39.16) * mm, v(-11, -52.26) * mm, v(0, -55.07) * mm], "startDerivative": vector(0, -14.28) * mm, "endDerivative": vector(23.36, -3.95) * mm});
            skLineSegment(sketch, "E220", {"start": v(-19.23, -25.48) * mm, "end": v(-11.25, -22.18) * mm});
            skLineSegment(sketch, "E221", {"start": v(-10.76, -19.74) * mm, "end": v(-11.64, -18.86) * mm});
            skLineSegment(sketch, "E222", {"start": v(-12.33, -18.84) * mm, "end": v(-12.35, -18.85) * mm});
            skLineSegment(sketch, "E223", {"start": v(-20.32, -23.85) * mm, "end": v(-16.5, -20.04) * mm});
            skLineSegment(sketch, "E224", {"start": v(-15.85, -19.83) * mm, "end": v(-15.74, -19.85) * mm});
            skPoint(sketch, "E225.visualSharp", {"position": v(-9.18, -21.32) * mm});
            skArc(sketch, "E225.filletArc", {"start": v(-11.25, -22.18) * mm, "mid": v(-10.35, -21.1) * mm, "end": v(-10.76, -19.74) * mm});
            skPoint(sketch, "E226.visualSharp", {"position": v(-11.98, -18.52) * mm});
            skArc(sketch, "E226.filletArc", {"start": v(-11.64, -18.86) * mm, "mid": v(-11.98, -18.7) * mm, "end": v(-12.33, -18.84) * mm});
            skPoint(sketch, "E227.visualSharp", {"position": v(-16.23, -19.77) * mm});
            skArc(sketch, "E227.filletArc", {"start": v(-15.85, -19.83) * mm, "mid": v(-16.2, -19.86) * mm, "end": v(-16.5, -20.04) * mm});
            skPoint(sketch, "E228.visualSharp", {"position": v(-23.87, -27.4) * mm});
            skArc(sketch, "E228.filletArc", {"start": v(-20.32, -23.85) * mm, "mid": v(-20.44, -25.11) * mm, "end": v(-19.23, -25.48) * mm});
            skLineSegment(sketch, "E229", {"start": v(15.25, -15.25) * mm, "end": v(9.18, -21.32) * mm, "construction": true});
            skLineSegment(sketch, "E230", {"start": v(11.14, -14.67) * mm, "end": v(23.87, -27.4) * mm, "construction": true});
            skLineSegment(sketch, "E231", {"start": v(19.23, -25.48) * mm, "end": v(11.25, -22.18) * mm});
            skLineSegment(sketch, "E232", {"start": v(10.76, -19.74) * mm, "end": v(11.64, -18.86) * mm});
            skLineSegment(sketch, "E233", {"start": v(12.33, -18.84) * mm, "end": v(12.35, -18.85) * mm});
            skLineSegment(sketch, "E234", {"start": v(20.32, -23.85) * mm, "end": v(16.5, -20.04) * mm});
            skLineSegment(sketch, "E235", {"start": v(15.85, -19.83) * mm, "end": v(15.74, -19.85) * mm});
            skPoint(sketch, "E236", {"position": v(13.76, -19.63) * mm});
            skArc(sketch, "E237", {"start": v(12.35, -18.85) * mm, "mid": v(13.95, -19.69) * mm, "end": v(15.74, -19.85) * mm});
            skPoint(sketch, "E238.visualSharp", {"position": v(9.18, -21.32) * mm});
            skArc(sketch, "E238.filletArc", {"start": v(10.76, -19.74) * mm, "mid": v(10.35, -21.1) * mm, "end": v(11.25, -22.18) * mm});
            skPoint(sketch, "E239.visualSharp", {"position": v(11.98, -18.52) * mm});
            skArc(sketch, "E239.filletArc", {"start": v(12.33, -18.84) * mm, "mid": v(11.98, -18.7) * mm, "end": v(11.64, -18.86) * mm});
            skPoint(sketch, "E240.visualSharp", {"position": v(23.87, -27.4) * mm});
            skArc(sketch, "E240.filletArc", {"start": v(19.23, -25.48) * mm, "mid": v(20.44, -25.11) * mm, "end": v(20.32, -23.85) * mm});
            skPoint(sketch, "E241.visualSharp", {"position": v(16.23, -19.77) * mm});
            skArc(sketch, "E241.filletArc", {"start": v(16.5, -20.04) * mm, "mid": v(16.2, -19.86) * mm, "end": v(15.85, -19.83) * mm});
            skPoint(sketch, "E242", {"position": v(-14.29, -19.77) * mm});
            skArc(sketch, "E243", {"start": v(-15.74, -19.85) * mm, "mid": v(-13.95, -19.69) * mm, "end": v(-12.35, -18.85) * mm});
            skLineSegment(sketch, "E244", {"start": v(-12.99, -49.05) * mm, "end": v(-7.99, -49.05) * mm, "construction": true});
            skLineSegment(sketch, "E245", {"start": v(-7.99, -49.05) * mm, "end": v(-7.99, -54.05) * mm, "construction": true});
            skLineSegment(sketch, "E246", {"start": v(12.99, -49.05) * mm, "end": v(7.99, -49.05) * mm, "construction": true});
            skLineSegment(sketch, "E247", {"start": v(7.99, -49.05) * mm, "end": v(7.99, -54.05) * mm, "construction": true});
            skCircle(sketch, "E248", {"center": v(7.99, -49.05) * mm, "radius": 1.5 * mm});
            skCircle(sketch, "E249", {"center": v(-7.99, -49.05) * mm, "radius": 1.5 * mm});
            skLineSegment(sketch, "E250", {"start": v(-8.94, 14.6) * mm, "end": v(-8.94, 19.63) * mm, "construction": true});
            skLineSegment(sketch, "E251", {"start": v(8.94, 14.6) * mm, "end": v(8.94, 19.63) * mm, "construction": true});
            skPoint(sketch, "E252", {"position": v(0, 21.57) * mm});
            skLineSegment(sketch, "E253", {"start": v(-7.77, 15.25) * mm, "end": v(-7.77, 20.12) * mm, "construction": true});
            skLineSegment(sketch, "E254", {"start": v(7.79, 15.24) * mm, "end": v(7.79, 20.11) * mm, "construction": true});
            skLineSegment(sketch, "E255", {"start": v(-8.94, 19.63) * mm, "end": v(-8.94, 22.43) * mm, "construction": true});
            skLineSegment(sketch, "E256", {"start": v(8.94, 19.63) * mm, "end": v(8.94, 22.43) * mm, "construction": true});
            skLineSegment(sketch, "E257", {"start": v(-8.94, 22.43) * mm, "end": v(-1.06, 27.36) * mm});
            skLineSegment(sketch, "E258", {"start": v(1.06, 27.36) * mm, "end": v(8.94, 22.43) * mm});
            skArc(sketch, "E259", {"start": v(-8.94, 22.43) * mm, "mid": v(-9.4, 20.74) * mm, "end": v(-7.77, 20.12) * mm});
            skArc(sketch, "E260", {"start": v(7.79, 20.11) * mm, "mid": v(9.41, 20.75) * mm, "end": v(8.94, 22.43) * mm});
            skPoint(sketch, "E261.visualSharp", {"position": v(0, 28.02) * mm});
            skArc(sketch, "E261.filletArc", {"start": v(1.06, 27.36) * mm, "mid": v(0, 27.66) * mm, "end": v(-1.06, 27.36) * mm});
            skArc(sketch, "E262", {"start": v(7.79, 20.11) * mm, "mid": v(0, 21.57) * mm, "end": v(-7.77, 20.12) * mm});
            skLineSegment(sketch, "E263", {"start": v(-8.94, -14.6) * mm, "end": v(-8.94, -19.63) * mm, "construction": true});
            skLineSegment(sketch, "E264", {"start": v(-7.77, -15.25) * mm, "end": v(-7.77, -20.12) * mm, "construction": true});
            skLineSegment(sketch, "E265", {"start": v(7.79, -15.24) * mm, "end": v(7.79, -20.11) * mm, "construction": true});
            skLineSegment(sketch, "E266", {"start": v(8.94, -14.6) * mm, "end": v(8.94, -19.63) * mm, "construction": true});
            skLineSegment(sketch, "E267", {"start": v(-8.94, -19.63) * mm, "end": v(-8.94, -22.43) * mm, "construction": true});
            skLineSegment(sketch, "E268", {"start": v(8.94, -19.63) * mm, "end": v(8.94, -22.43) * mm, "construction": true});
            skPoint(sketch, "E269", {"position": v(0, -26.25) * mm});
            skPoint(sketch, "E270.visualSharp", {"position": v(0, -30.25) * mm});
            skPoint(sketch, "E271", {"position": v(0, -24.5) * mm});
            skLineSegment(sketch, "E272", {"start": v(0, -26.25) * mm, "end": v(-11.25, -26.25) * mm, "construction": true});
            skLineSegment(sketch, "E273", {"start": v(0, -26.25) * mm, "end": v(11.25, -26.25) * mm, "construction": true});
            skPoint(sketch, "E274.visualSharp", {"position": v(-11.25, -26.25) * mm});
            skPoint(sketch, "E275.visualSharp", {"position": v(11.25, -26.25) * mm});
            skPoint(sketch, "E276.visualSharp", {"position": v(0, -37.76) * mm});
            skPoint(sketch, "E277", {"position": v(0, -39.7) * mm});
            skLineSegment(sketch, "E278", {"start": v(-9.19, -28.72) * mm, "end": v(-1.34, -38.1) * mm});
            skLineSegment(sketch, "E279", {"start": v(1.34, -38.1) * mm, "end": v(9.19, -28.72) * mm});
            skLineSegment(sketch, "E280", {"start": v(-8.04, -26.25) * mm, "end": v(8.04, -26.25) * mm});
            skArc(sketch, "E281.filletArc", {"start": v(-8.04, -26.25) * mm, "mid": v(-9.4, -27.12) * mm, "end": v(-9.19, -28.72) * mm});
            skArc(sketch, "E282.filletArc", {"start": v(9.19, -28.72) * mm, "mid": v(9.4, -27.12) * mm, "end": v(8.04, -26.25) * mm});
            skArc(sketch, "E283.filletArc", {"start": v(-1.34, -38.1) * mm, "mid": v(0, -38.72) * mm, "end": v(1.34, -38.1) * mm});
            skLineSegment(sketch, "E284", {"start": v(0, 34) * mm, "end": v(8.73, 34) * mm, "construction": true});
            skLineSegment(sketch, "E285", {"start": v(0, 34) * mm, "end": v(-8.73, 34) * mm, "construction": true});
            skLineSegment(sketch, "E286", {"start": v(0, 37.76) * mm, "end": v(0, 47.76) * mm, "construction": true});
            skLineSegment(sketch, "E287", {"start": v(0, 47.76) * mm, "end": v(-15, 47.76) * mm, "construction": true});
            skLineSegment(sketch, "E288", {"start": v(0, 47.76) * mm, "end": v(15, 47.76) * mm, "construction": true});
            skLineSegment(sketch, "E289", {"start": v(0, 47.76) * mm, "end": v(-13, 47.76) * mm});
            skLineSegment(sketch, "E290", {"start": v(-15, 45.76) * mm, "end": v(-15.03, 35.79) * mm});
            skLineSegment(sketch, "E291", {"start": v(0, 47.76) * mm, "end": v(13, 47.76) * mm});
            skLineSegment(sketch, "E292", {"start": v(15, 45.76) * mm, "end": v(15.03, 35.79) * mm});
            skPoint(sketch, "E293.visualSharp", {"position": v(-15, 47.76) * mm});
            skArc(sketch, "E293.filletArc", {"start": v(-13, 47.76) * mm, "mid": v(-14.42, 47.17) * mm, "end": v(-15, 45.76) * mm});
            skPoint(sketch, "E294.visualSharp", {"position": v(15, 47.76) * mm});
            skArc(sketch, "E294.filletArc", {"start": v(15, 45.76) * mm, "mid": v(14.42, 47.17) * mm, "end": v(13, 47.76) * mm});
            skLineSegment(sketch, "E295", {"start": v(11.5, 37.76) * mm, "end": v(11.5, 43.96) * mm, "construction": true});
            skLineSegment(sketch, "E296", {"start": v(11.5, 43.96) * mm, "end": v(-11.5, 43.96) * mm, "construction": true});
            skLineSegment(sketch, "E297", {"start": v(-15, -39.16) * mm, "end": v(0, -39.16) * mm, "construction": true});
            skLineSegment(sketch, "E298", {"start": v(0, -39.16) * mm, "end": v(15, -39.15) * mm, "construction": true});
            skSolve(sketch);
        }
        {
            var Q0;
            Q0=qCreatedBy(makeId("Top.planeOp"),FACE);
            var sketch = newSketch(context, id + "F1", { "sketchPlane" : qUnion([Q0])});
            skLineSegment(sketch, "E299.bottom", {"start": v(-15.24, 15.25) * mm, "end": v(15.26, 15.25) * mm, "construction": true});
            skLineSegment(sketch, "E299.top", {"start": v(-15.24, -15.25) * mm, "end": v(15.26, -15.25) * mm, "construction": true});
            skLineSegment(sketch, "E299.left", {"start": v(-15.24, 15.25) * mm, "end": v(-15.24, -15.25) * mm, "construction": true});
            skLineSegment(sketch, "E299.right", {"start": v(15.26, 15.25) * mm, "end": v(15.26, -15.25) * mm, "construction": true});
            skPoint(sketch, "E299.middle", {"position": v(0, 0) * mm});
            skLineSegment(sketch, "E300.bottom", {"start": v(30.26, 30.25) * mm, "end": v(-30.24, 30.25) * mm, "construction": true});
            skLineSegment(sketch, "E300.top", {"start": v(30.26, -30.25) * mm, "end": v(-30.24, -30.25) * mm, "construction": true});
            skLineSegment(sketch, "E300.left", {"start": v(30.26, 30.25) * mm, "end": v(30.26, -30.25) * mm, "construction": true});
            skLineSegment(sketch, "E300.right", {"start": v(-30.24, 30.25) * mm, "end": v(-30.24, -30.25) * mm, "construction": true});
            skLineSegment(sketch, "E301.bottom", {"start": v(-74.24, 74.25) * mm, "end": v(74.25, 74.25) * mm, "construction": true});
            skLineSegment(sketch, "E301.top", {"start": v(-74.24, -74.24) * mm, "end": v(74.25, -74.24) * mm, "construction": true});
            skLineSegment(sketch, "E301.left", {"start": v(-74.24, 74.25) * mm, "end": v(-74.24, -74.24) * mm, "construction": true});
            skLineSegment(sketch, "E301.right", {"start": v(74.25, 74.25) * mm, "end": v(74.25, -74.24) * mm, "construction": true});
            skCircle(sketch, "E302", {"center": v(74.25, 74.25) * mm, "radius": 4.5 * mm});
            skCircle(sketch, "E303", {"center": v(-74.24, 74.25) * mm, "radius": 4.5 * mm, "construction": true});
            skCircle(sketch, "E304", {"center": v(74.25, -74.24) * mm, "radius": 4.5 * mm, "construction": true});
            skCircle(sketch, "E305", {"center": v(-74.24, -74.24) * mm, "radius": 4.5 * mm, "construction": true});
            skCircle(sketch, "E306", {"center": v(74.25, 74.25) * mm, "radius": 8 * mm, "construction": true});
            skCircle(sketch, "E307", {"center": v(74.25, -74.24) * mm, "radius": 8 * mm, "construction": true});
            skCircle(sketch, "E308", {"center": v(-74.24, -74.24) * mm, "radius": 8 * mm, "construction": true});
            skCircle(sketch, "E309", {"center": v(-74.24, 74.25) * mm, "radius": 8 * mm, "construction": true});
            skCircle(sketch, "E310", {"center": v(74.25, 74.25) * mm, "radius": 9.5 * mm, "construction": true});
            skCircle(sketch, "E311", {"center": v(74.25, -74.24) * mm, "radius": 9.5 * mm, "construction": true});
            skCircle(sketch, "E312", {"center": v(-74.24, -74.24) * mm, "radius": 9.5 * mm, "construction": true});
            skCircle(sketch, "E313", {"center": v(-74.24, 74.25) * mm, "radius": 9.5 * mm, "construction": true});
            skCircle(sketch, "E314", {"center": v(74.25, 74.25) * mm, "radius": 14 * mm, "construction": true});
            skCircle(sketch, "E315", {"center": v(-74.24, 74.25) * mm, "radius": 14 * mm, "construction": true});
            skCircle(sketch, "E316", {"center": v(74.25, -74.24) * mm, "radius": 14 * mm, "construction": true});
            skCircle(sketch, "E317", {"center": v(-74.24, -74.24) * mm, "radius": 14 * mm, "construction": true});
            skCircle(sketch, "E318", {"center": v(74.25, 74.25) * mm, "radius": 63.5 * mm, "construction": true});
            skCircle(sketch, "E319", {"center": v(74.25, -74.24) * mm, "radius": 63.5 * mm, "construction": true});
            skCircle(sketch, "E320", {"center": v(-74.24, -74.24) * mm, "radius": 63.5 * mm, "construction": true});
            skCircle(sketch, "E321", {"center": v(-74.24, 74.25) * mm, "radius": 63.5 * mm, "construction": true});
            skLineSegment(sketch, "E322", {"start": v(0, 30.25) * mm, "end": v(0, 36.4) * mm, "construction": true});
            skLineSegment(sketch, "E323", {"start": v(0, 36.4) * mm, "end": v(-14.28, 36.4) * mm, "construction": true});
            skLineSegment(sketch, "E324", {"start": v(0, 36.4) * mm, "end": v(14.3, 36.4) * mm, "construction": true});
            skLineSegment(sketch, "E325", {"start": v(0, -30.25) * mm, "end": v(0, -36.4) * mm, "construction": true});
            skLineSegment(sketch, "E326", {"start": v(0, -36.4) * mm, "end": v(-14.28, -36.4) * mm, "construction": true});
            skLineSegment(sketch, "E327", {"start": v(0, -36.4) * mm, "end": v(14.3, -36.4) * mm, "construction": true});
            skLineSegment(sketch, "E328.bottom", {"start": v(-26.18, 26.2) * mm, "end": v(26.2, 26.2) * mm, "construction": true});
            skLineSegment(sketch, "E328.top", {"start": v(-26.18, -26.19) * mm, "end": v(26.2, -26.19) * mm, "construction": true});
            skLineSegment(sketch, "E328.left", {"start": v(-26.18, 26.2) * mm, "end": v(-26.18, -26.19) * mm, "construction": true});
            skLineSegment(sketch, "E328.right", {"start": v(26.2, 26.2) * mm, "end": v(26.2, -26.19) * mm, "construction": true});
            skCircle(sketch, "E329", {"center": v(30.26, 30.25) * mm, "radius": 7.5 * mm, "construction": true});
            skCircle(sketch, "E330", {"center": v(-30.24, 30.25) * mm, "radius": 7.5 * mm, "construction": true});
            skCircle(sketch, "E331", {"center": v(30.26, -30.25) * mm, "radius": 7.5 * mm, "construction": true});
            skCircle(sketch, "E332", {"center": v(-30.24, -30.25) * mm, "radius": 7.5 * mm, "construction": true});
            skCircle(sketch, "E333", {"center": v(15.26, 15.25) * mm, "radius": 1.5 * mm, "construction": true});
            skCircle(sketch, "E334", {"center": v(-15.24, 15.25) * mm, "radius": 1.5 * mm, "construction": true});
            skCircle(sketch, "E335", {"center": v(15.26, -15.25) * mm, "radius": 1.5 * mm, "construction": true});
            skCircle(sketch, "E336", {"center": v(-15.24, -15.25) * mm, "radius": 1.5 * mm, "construction": true});
            skLineSegment(sketch, "E337", {"start": v(15.26, 15.25) * mm, "end": v(0, 0) * mm, "construction": true});
            skLineSegment(sketch, "E338", {"start": v(-15.24, 15.25) * mm, "end": v(0, 0) * mm, "construction": true});
            skLineSegment(sketch, "E339", {"start": v(15.26, -15.25) * mm, "end": v(0, 0) * mm, "construction": true});
            skLineSegment(sketch, "E340", {"start": v(-15.24, -15.25) * mm, "end": v(0, 0) * mm, "construction": true});
            skCircle(sketch, "E341", {"center": v(15.26, 15.25) * mm, "radius": 5 * mm, "construction": true});
            skCircle(sketch, "E342", {"center": v(-15.24, 15.25) * mm, "radius": 5 * mm, "construction": true});
            skCircle(sketch, "E343", {"center": v(-15.24, -15.25) * mm, "radius": 5 * mm, "construction": true});
            skCircle(sketch, "E344", {"center": v(15.26, -15.25) * mm, "radius": 5 * mm, "construction": true});
            skLineSegment(sketch, "E345.bottom", {"start": v(-5.65, -5.65) * mm, "end": v(5.66, -5.65) * mm, "construction": true});
            skLineSegment(sketch, "E345.top", {"start": v(-5.65, 5.66) * mm, "end": v(5.66, 5.66) * mm, "construction": true});
            skLineSegment(sketch, "E345.left", {"start": v(-5.65, -5.65) * mm, "end": v(-5.65, 5.66) * mm, "construction": true});
            skLineSegment(sketch, "E345.right", {"start": v(5.66, -5.65) * mm, "end": v(5.66, 5.66) * mm, "construction": true});
            skPoint(sketch, "E346", {"position": v(0, 5.66) * mm});
            skPoint(sketch, "E347", {"position": v(5.66, 0) * mm});
            skPoint(sketch, "E348", {"position": v(-5.65, 0) * mm});
            skPoint(sketch, "E349", {"position": v(0, -5.65) * mm});
            skLineSegment(sketch, "E350", {"start": v(15.26, 15.25) * mm, "end": v(74.25, 74.25) * mm, "construction": true});
            skLineSegment(sketch, "E351", {"start": v(64.35, 64.35) * mm, "end": v(59.4, 69.3) * mm, "construction": true});
            skLineSegment(sketch, "E352", {"start": v(64.35, 64.35) * mm, "end": v(69.3, 59.4) * mm, "construction": true});
            skCircle(sketch, "E353", {"center": v(74.25, 74.25) * mm, "radius": 23.5 * mm, "construction": true});
            skLineSegment(sketch, "E354", {"start": v(74.25, 74.25) * mm, "end": v(74.25, 97.75) * mm, "construction": true});
            skLineSegment(sketch, "E355", {"start": v(74.25, 74.25) * mm, "end": v(97.75, 74.25) * mm, "construction": true});
            skLineSegment(sketch, "E356", {"start": v(53.84, 63.73) * mm, "end": v(27.21, 37.1) * mm});
            skLineSegment(sketch, "E357", {"start": v(66.94, 57.03) * mm, "end": v(37.11, 27.2) * mm});
            skCircle(sketch, "E358", {"center": v(74.25, 74.25) * mm, "radius": 15.5 * mm, "construction": true});
            skLineSegment(sketch, "E359", {"start": v(74.25, 74.25) * mm, "end": v(57.64, 90.86) * mm, "construction": true});
            skLineSegment(sketch, "E360", {"start": v(74.25, 74.25) * mm, "end": v(90.87, 57.63) * mm, "construction": true});
            skLineSegment(sketch, "E361", {"start": v(74.25, 74.25) * mm, "end": v(90.87, 90.86) * mm, "construction": true});
            skLineSegment(sketch, "E362", {"start": v(90.87, 57.63) * mm, "end": v(96.28, 66.04) * mm, "construction": true});
            skLineSegment(sketch, "E363", {"start": v(90.87, 90.86) * mm, "end": v(94.01, 86.97) * mm, "construction": true});
            skLineSegment(sketch, "E364", {"start": v(90.87, 90.86) * mm, "end": v(86.98, 94) * mm, "construction": true});
            skLineSegment(sketch, "E365", {"start": v(57.64, 90.86) * mm, "end": v(66.05, 96.27) * mm, "construction": true});
            skCircle(sketch, "E366", {"center": v(74.25, 74.25) * mm, "radius": 20 * mm, "construction": true});
            skLineSegment(sketch, "E367", {"start": v(66.05, 96.27) * mm, "end": v(68, 93.24) * mm, "construction": true});
            skLineSegment(sketch, "E368", {"start": v(86.98, 94) * mm, "end": v(84.77, 91.26) * mm, "construction": true});
            skLineSegment(sketch, "E369", {"start": v(94.01, 86.97) * mm, "end": v(91.27, 84.76) * mm, "construction": true});
            skPoint(sketch, "E370", {"position": v(60.11, 88.39) * mm});
            skPoint(sketch, "E371", {"position": v(61.84, 93.56) * mm});
            skLineSegment(sketch, "E372", {"start": v(68, 93.24) * mm, "end": v(84.77, 91.26) * mm, "construction": true});
            skLineSegment(sketch, "E373", {"start": v(76.38, 92.25) * mm, "end": v(76.07, 89.64) * mm, "construction": true});
            skLineSegment(sketch, "E374", {"start": v(76.07, 89.64) * mm, "end": v(75.9, 88.15) * mm, "construction": true});
            skPoint(sketch, "E375", {"position": v(93.57, 61.83) * mm});
            skLineSegment(sketch, "E376", {"start": v(96.28, 66.04) * mm, "end": v(93.25, 67.99) * mm, "construction": true});
            skPoint(sketch, "E377", {"position": v(88.4, 60.1) * mm});
            skPoint(sketch, "E378.visualSharp", {"position": v(60.25, 74.25) * mm});
            skPoint(sketch, "E379.visualSharp", {"position": v(75.9, 88.15) * mm});
            skPoint(sketch, "E380.visualSharp", {"position": v(88.25, 74.25) * mm});
            skPoint(sketch, "E381.visualSharp", {"position": v(74.25, 60.12) * mm});
            skPoint(sketch, "E382.visualSharp", {"position": v(59.4, 69.3) * mm});
            skPoint(sketch, "E383.visualSharp", {"position": v(69.3, 59.4) * mm});
            skLineSegment(sketch, "E384", {"start": v(79.91, 79.9) * mm, "end": v(83.1, 83.08) * mm, "construction": true});
            skLineSegment(sketch, "E385", {"start": v(74.25, 93.54) * mm, "end": v(69, 93.54) * mm, "construction": true});
            skLineSegment(sketch, "E386", {"start": v(74.25, 93.54) * mm, "end": v(79.5, 93.54) * mm, "construction": true});
            skFitSpline(sketch, "E387", {"points": [v(69, 93.54) * mm, v(74.25, 97.75) * mm, v(79.5, 93.54) * mm], "startDerivative": vector(9, 14.06) * mm, "endDerivative": vector(9, -14.06) * mm});
            skLineSegment(sketch, "E388", {"start": v(74.25, 95.89) * mm, "end": v(78, 95.89) * mm, "construction": true});
            skLineSegment(sketch, "E389", {"start": v(74.25, 95.89) * mm, "end": v(70.5, 95.89) * mm, "construction": true});
            skLineSegment(sketch, "E390", {"start": v(69, 93.54) * mm, "end": v(64.35, 84.14) * mm});
            skPoint(sketch, "E391", {"position": v(61.23, 79.38) * mm});
            skArc(sketch, "E392", {"start": v(64.35, 84.14) * mm, "mid": v(61.32, 79.6) * mm, "end": v(60.25, 74.25) * mm});
            skPoint(sketch, "E393", {"position": v(87.37, 79.13) * mm});
            skFitSpline(sketch, "E394", {"points": [v(87.37, 79.13) * mm, v(94.25, 74.25) * mm, v(71.77, 58.94) * mm], "startDerivative": vector(24.48, -10.1) * mm, "endDerivative": vector(-49.92, -7.72) * mm});
            skFitSpline(sketch, "E395", {"points": [v(53.84, 63.73) * mm, v(60.25, 74.25) * mm], "startDerivative": vector(4.73, 4.42) * mm, "endDerivative": vector(1.47, 12.68) * mm});
            skLineSegment(sketch, "E396", {"start": v(16.8, 16.8) * mm, "end": v(13.62, 19.97) * mm, "construction": true});
            skLineSegment(sketch, "E397", {"start": v(16.8, 16.8) * mm, "end": v(19.98, 13.6) * mm, "construction": true});
            skLineSegment(sketch, "E398", {"start": v(37.11, 27.2) * mm, "end": v(33.3, 23.4) * mm, "construction": true});
            skLineSegment(sketch, "E399", {"start": v(27.21, 37.1) * mm, "end": v(23.4, 33.3) * mm, "construction": true});
            skLineSegment(sketch, "E400", {"start": v(23.4, 33.3) * mm, "end": v(13.62, 19.97) * mm});
            skLineSegment(sketch, "E401", {"start": v(33.3, 23.4) * mm, "end": v(19.98, 13.6) * mm});
            skPoint(sketch, "E402", {"position": v(25.01, 35.61) * mm});
            skPoint(sketch, "E403", {"position": v(35.69, 25.07) * mm});
            skArc(sketch, "E404", {"start": v(33.3, 23.4) * mm, "mid": v(35.56, 24.95) * mm, "end": v(37.11, 27.2) * mm});
            skArc(sketch, "E405", {"start": v(27.21, 37.1) * mm, "mid": v(24.96, 35.55) * mm, "end": v(23.4, 33.3) * mm});
            skLineSegment(sketch, "E406.bottom", {"start": v(0, 5.66) * mm, "end": v(6.37, 5.66) * mm, "construction": true});
            skLineSegment(sketch, "E406.top", {"start": v(0, 12.02) * mm, "end": v(6.37, 12.02) * mm, "construction": true});
            skLineSegment(sketch, "E406.left", {"start": v(0, 5.66) * mm, "end": v(0, 12.02) * mm, "construction": true});
            skLineSegment(sketch, "E406.right", {"start": v(6.37, 5.66) * mm, "end": v(6.37, 12.02) * mm, "construction": true});
            skLineSegment(sketch, "E407", {"start": v(0, 5.66) * mm, "end": v(6.37, 12.02) * mm});
            skLineSegment(sketch, "E408", {"start": v(6.37, 12.02) * mm, "end": v(10.3, 15.95) * mm});
            skLineSegment(sketch, "E409.bottom", {"start": v(5.66, 0) * mm, "end": v(12.02, 0) * mm, "construction": true});
            skLineSegment(sketch, "E409.top", {"start": v(5.66, 6.36) * mm, "end": v(12.02, 6.36) * mm, "construction": true});
            skLineSegment(sketch, "E409.left", {"start": v(5.66, 0) * mm, "end": v(5.66, 6.36) * mm, "construction": true});
            skLineSegment(sketch, "E409.right", {"start": v(12.02, 0) * mm, "end": v(12.02, 6.36) * mm, "construction": true});
            skLineSegment(sketch, "E410", {"start": v(5.66, 0) * mm, "end": v(12.02, 6.36) * mm});
            skLineSegment(sketch, "E411", {"start": v(12.02, 6.36) * mm, "end": v(15.96, 10.3) * mm});
            skPoint(sketch, "E412", {"position": v(11.75, 18.81) * mm});
            skPoint(sketch, "E413", {"position": v(19.05, 11.99) * mm});
            skArc(sketch, "E414", {"start": v(15.96, 10.3) * mm, "mid": v(18.44, 11.4) * mm, "end": v(19.98, 13.6) * mm});
            skArc(sketch, "E415", {"start": v(13.62, 19.97) * mm, "mid": v(11.4, 18.43) * mm, "end": v(10.3, 15.95) * mm});
            skLineSegment(sketch, "E416", {"start": v(0, 5.66) * mm, "end": v(0, 0) * mm});
            skLineSegment(sketch, "E417", {"start": v(0, 0) * mm, "end": v(5.66, 0) * mm});
            skCircle(sketch, "E418", {"center": v(30.26, 30.25) * mm, "radius": 1.5 * mm});
            skCircle(sketch, "E419", {"center": v(15.26, 15.25) * mm, "radius": 1.5 * mm});
            skPoint(sketch, "E420", {"position": v(74.25, 94.25) * mm});
            skLineSegment(sketch, "E421", {"start": v(74.25, 89.74) * mm, "end": v(70.58, 89.3) * mm, "construction": true});
            skLineSegment(sketch, "E422", {"start": v(74.25, 89.74) * mm, "end": v(77.93, 89.3) * mm, "construction": true});
            skLineSegment(sketch, "E423", {"start": v(77.93, 89.3) * mm, "end": v(79.1, 87.38) * mm, "construction": true});
            skLineSegment(sketch, "E424", {"start": v(70.58, 89.3) * mm, "end": v(69.41, 87.38) * mm, "construction": true});
            skPoint(sketch, "E425", {"position": v(79.1, 87.38) * mm});
            skPoint(sketch, "E426", {"position": v(69.41, 87.38) * mm});
            skPoint(sketch, "E427", {"position": v(74.25, 92.5) * mm});
            skLineSegment(sketch, "E428", {"start": v(70.58, 89.3) * mm, "end": v(70.76, 87.8) * mm, "construction": true});
            skLineSegment(sketch, "E429", {"start": v(77.93, 89.3) * mm, "end": v(77.75, 87.8) * mm, "construction": true});
            skLineSegment(sketch, "E430", {"start": v(70.76, 87.8) * mm, "end": v(70.88, 86.8) * mm, "construction": true});
            skLineSegment(sketch, "E431", {"start": v(77.75, 87.8) * mm, "end": v(77.63, 86.8) * mm, "construction": true});
            skFitSpline(sketch, "E432", {"points": [v(70.76, 87.8) * mm, v(74.25, 92.5) * mm, v(77.75, 87.8) * mm], "startDerivative": vector(6.99, 14.1) * mm, "endDerivative": vector(6.99, -14.1) * mm});
            skLineSegment(sketch, "E433", {"start": v(70.88, 86.8) * mm, "end": v(77.63, 86.8) * mm, "construction": true});
            skPoint(sketch, "E434", {"position": v(74.25, 86.8) * mm});
            skFitSpline(sketch, "E435", {"points": [v(70.76, 87.8) * mm, v(74.25, 86.8) * mm, v(77.75, 87.8) * mm], "startDerivative": vector(0.72, -5.96) * mm, "endDerivative": vector(0.72, 5.96) * mm});
            skCircle(sketch, "E436", {"center": v(74.25, 82.25) * mm, "radius": 1.5 * mm, "construction": true});
            skCircle(sketch, "E437", {"center": v(74.25, 83.75) * mm, "radius": 1.5 * mm, "construction": true});
            skCircle(sketch, "E438", {"center": v(82.25, 74.25) * mm, "radius": 1.5 * mm, "construction": true});
            skCircle(sketch, "E439", {"center": v(83.75, 74.25) * mm, "radius": 1.5 * mm, "construction": true});
            skCircle(sketch, "E440", {"center": v(74.25, 66.25) * mm, "radius": 1.5 * mm, "construction": true});
            skCircle(sketch, "E441", {"center": v(74.25, 64.75) * mm, "radius": 1.5 * mm, "construction": true});
            skCircle(sketch, "E442", {"center": v(66.25, 74.25) * mm, "radius": 1.5 * mm, "construction": true});
            skCircle(sketch, "E443", {"center": v(64.75, 74.25) * mm, "radius": 1.5 * mm, "construction": true});
            skPoint(sketch, "E444", {"position": v(75.55, 83) * mm});
            skPoint(sketch, "E445", {"position": v(72.96, 83) * mm});
            skPoint(sketch, "E446", {"position": v(74.25, 85.25) * mm});
            skPoint(sketch, "E447", {"position": v(74.25, 80.75) * mm});
            skArc(sketch, "E448", {"start": v(72.96, 83) * mm, "mid": v(74.25, 80.75) * mm, "end": v(75.55, 83) * mm});
            skArc(sketch, "E449", {"start": v(75.55, 83) * mm, "mid": v(74.25, 85.25) * mm, "end": v(72.96, 83) * mm});
            skPoint(sketch, "E450", {"position": v(80.75, 74.25) * mm});
            skPoint(sketch, "E451", {"position": v(83, 75.54) * mm});
            skPoint(sketch, "E452", {"position": v(83, 72.95) * mm});
            skPoint(sketch, "E453", {"position": v(85.25, 74.25) * mm});
            skPoint(sketch, "E454", {"position": v(74.25, 63.25) * mm});
            skPoint(sketch, "E455", {"position": v(74.25, 67.75) * mm});
            skPoint(sketch, "E456", {"position": v(72.96, 65.5) * mm});
            skPoint(sketch, "E457", {"position": v(75.55, 65.5) * mm});
            skPoint(sketch, "E458", {"position": v(65.5, 75.54) * mm});
            skPoint(sketch, "E459", {"position": v(65.5, 72.95) * mm});
            skPoint(sketch, "E460", {"position": v(63.25, 74.25) * mm});
            skPoint(sketch, "E461", {"position": v(67.75, 74.25) * mm});
            skArc(sketch, "E462", {"start": v(65.5, 72.95) * mm, "mid": v(67.75, 74.25) * mm, "end": v(65.5, 75.54) * mm});
            skArc(sketch, "E463", {"start": v(65.5, 75.54) * mm, "mid": v(63.25, 74.25) * mm, "end": v(65.5, 72.95) * mm});
            skArc(sketch, "E464", {"start": v(83, 75.54) * mm, "mid": v(80.75, 74.25) * mm, "end": v(83, 72.95) * mm});
            skArc(sketch, "E465", {"start": v(83, 72.95) * mm, "mid": v(85.25, 74.25) * mm, "end": v(83, 75.54) * mm});
            skArc(sketch, "E466", {"start": v(72.96, 65.5) * mm, "mid": v(74.25, 63.25) * mm, "end": v(75.55, 65.5) * mm});
            skArc(sketch, "E467", {"start": v(75.55, 65.5) * mm, "mid": v(74.25, 67.75) * mm, "end": v(72.96, 65.5) * mm});
            skLineSegment(sketch, "E468", {"start": v(79.5, 93.54) * mm, "end": v(84.15, 84.14) * mm});
            skPoint(sketch, "E469", {"position": v(86.02, 81.83) * mm});
            skArc(sketch, "E470", {"start": v(87.37, 79.13) * mm, "mid": v(86.03, 81.81) * mm, "end": v(84.15, 84.14) * mm});
            skPoint(sketch, "E471", {"position": v(88.23, 75.07) * mm});
            skPoint(sketch, "E472", {"position": v(89.75, 74.25) * mm});
            skPoint(sketch, "E473", {"position": v(84.32, 67.22) * mm});
            skFitSpline(sketch, "E474", {"points": [v(88.23, 75.07) * mm, v(89.75, 74.25) * mm, v(84.32, 67.22) * mm], "startDerivative": vector(7.89, -0.55) * mm, "endDerivative": vector(-14.19, -5.55) * mm});
            skPoint(sketch, "E475", {"position": v(80.17, 74.71) * mm});
            skFitSpline(sketch, "E476", {"points": [v(84.32, 67.22) * mm, v(87.06, 74.25) * mm, v(88.23, 75.07) * mm], "startDerivative": vector(-5.21, -2.06) * mm, "endDerivative": vector(5.66, -0.3) * mm});
            skFitSpline(sketch, "E477", {"points": [v(66.94, 57.03) * mm, v(71.77, 58.94) * mm], "startDerivative": vector(5.12, 3.73) * mm, "endDerivative": vector(5.29, 1) * mm});
            skSolve(sketch);
        }
        {
            var Q0;
            Q0=qSketchRegion(id+"F0",true);
            extrude(context, id + "F2", {"entities" : qUnion([Q0]), "depth" : 2 * mm});
        }
        {
            var Q0;
            Q0=qCreatedBy(makeId("Top.planeOp"),FACE);
            var sketch = newSketch(context, id + "F3", { "sketchPlane" : qUnion([Q0])});
            skLineSegment(sketch, "E478.bottom", {"start": v(-15.25, 15.25) * mm, "end": v(15.25, 15.25) * mm, "construction": true});
            skLineSegment(sketch, "E478.top", {"start": v(-15.25, -15.25) * mm, "end": v(15.25, -15.25) * mm, "construction": true});
            skLineSegment(sketch, "E478.left", {"start": v(-15.25, 15.25) * mm, "end": v(-15.25, -15.25) * mm, "construction": true});
            skLineSegment(sketch, "E478.right", {"start": v(15.25, 15.25) * mm, "end": v(15.25, -15.25) * mm, "construction": true});
            skPoint(sketch, "E478.middle", {"position": v(0, 0) * mm});
            skLineSegment(sketch, "E479.bottom", {"start": v(30.25, 30.25) * mm, "end": v(-30.25, 30.25) * mm, "construction": true});
            skLineSegment(sketch, "E479.top", {"start": v(30.25, -30.25) * mm, "end": v(-30.25, -30.25) * mm, "construction": true});
            skLineSegment(sketch, "E479.left", {"start": v(30.25, 30.25) * mm, "end": v(30.25, -30.25) * mm, "construction": true});
            skLineSegment(sketch, "E479.right", {"start": v(-30.25, 30.25) * mm, "end": v(-30.25, -30.25) * mm, "construction": true});
            skLineSegment(sketch, "E480.bottom", {"start": v(-70.96, 70.96) * mm, "end": v(70.96, 70.96) * mm, "construction": true});
            skLineSegment(sketch, "E480.top", {"start": v(-70.96, -70.96) * mm, "end": v(70.96, -70.96) * mm, "construction": true});
            skLineSegment(sketch, "E480.left", {"start": v(-70.96, 70.96) * mm, "end": v(-70.96, -70.96) * mm, "construction": true});
            skLineSegment(sketch, "E480.right", {"start": v(70.96, 70.96) * mm, "end": v(70.96, -70.96) * mm, "construction": true});
            skCircle(sketch, "E481", {"center": v(70.96, 70.96) * mm, "radius": 4.5 * mm, "construction": true});
            skCircle(sketch, "E482", {"center": v(-70.96, 70.96) * mm, "radius": 4.5 * mm, "construction": true});
            skCircle(sketch, "E483", {"center": v(70.96, -70.96) * mm, "radius": 4.5 * mm, "construction": true});
            skCircle(sketch, "E484", {"center": v(-70.96, -70.96) * mm, "radius": 4.5 * mm, "construction": true});
            skCircle(sketch, "E485", {"center": v(70.96, 70.96) * mm, "radius": 8 * mm, "construction": true});
            skCircle(sketch, "E486", {"center": v(70.96, -70.96) * mm, "radius": 8 * mm, "construction": true});
            skCircle(sketch, "E487", {"center": v(-70.96, -70.96) * mm, "radius": 8 * mm, "construction": true});
            skCircle(sketch, "E488", {"center": v(-70.96, 70.96) * mm, "radius": 8 * mm, "construction": true});
            skCircle(sketch, "E489", {"center": v(70.96, 70.96) * mm, "radius": 9.5 * mm, "construction": true});
            skCircle(sketch, "E490", {"center": v(70.96, -70.96) * mm, "radius": 9.5 * mm, "construction": true});
            skCircle(sketch, "E491", {"center": v(-70.96, -70.96) * mm, "radius": 9.5 * mm, "construction": true});
            skCircle(sketch, "E492", {"center": v(-70.96, 70.96) * mm, "radius": 9.5 * mm, "construction": true});
            skCircle(sketch, "E493", {"center": v(70.96, 70.96) * mm, "radius": 14 * mm, "construction": true});
            skCircle(sketch, "E494", {"center": v(-70.96, 70.96) * mm, "radius": 14 * mm, "construction": true});
            skCircle(sketch, "E495", {"center": v(70.96, -70.96) * mm, "radius": 14 * mm, "construction": true});
            skCircle(sketch, "E496", {"center": v(-70.96, -70.96) * mm, "radius": 14 * mm, "construction": true});
            skCircle(sketch, "E497", {"center": v(70.96, 70.96) * mm, "radius": 63.5 * mm, "construction": true});
            skCircle(sketch, "E498", {"center": v(70.96, -70.96) * mm, "radius": 63.5 * mm, "construction": true});
            skCircle(sketch, "E499", {"center": v(-70.96, -70.96) * mm, "radius": 63.5 * mm, "construction": true});
            skCircle(sketch, "E500", {"center": v(-70.96, 70.96) * mm, "radius": 63.5 * mm, "construction": true});
            skLineSegment(sketch, "E501", {"start": v(0, 30.25) * mm, "end": v(0, 36.4) * mm, "construction": true});
            skLineSegment(sketch, "E502", {"start": v(0, 36.4) * mm, "end": v(-14.3, 36.4) * mm, "construction": true});
            skLineSegment(sketch, "E503", {"start": v(0, 36.4) * mm, "end": v(14.29, 36.4) * mm, "construction": true});
            skLineSegment(sketch, "E504", {"start": v(0, -30.25) * mm, "end": v(0, -36.4) * mm, "construction": true});
            skLineSegment(sketch, "E505", {"start": v(0, -36.4) * mm, "end": v(-14.29, -36.4) * mm, "construction": true});
            skLineSegment(sketch, "E506", {"start": v(0, -36.4) * mm, "end": v(14.3, -36.4) * mm, "construction": true});
            skLineSegment(sketch, "E507.bottom", {"start": v(-26.2, 26.2) * mm, "end": v(26.2, 26.2) * mm, "construction": true});
            skLineSegment(sketch, "E507.top", {"start": v(-26.2, -26.19) * mm, "end": v(26.2, -26.19) * mm, "construction": true});
            skLineSegment(sketch, "E507.left", {"start": v(-26.2, 26.2) * mm, "end": v(-26.2, -26.19) * mm, "construction": true});
            skLineSegment(sketch, "E507.right", {"start": v(26.2, 26.2) * mm, "end": v(26.2, -26.2) * mm, "construction": true});
            skCircle(sketch, "E508", {"center": v(30.25, 30.25) * mm, "radius": 5 * mm, "construction": true});
            skCircle(sketch, "E509", {"center": v(-30.25, 30.25) * mm, "radius": 5 * mm, "construction": true});
            skCircle(sketch, "E510", {"center": v(30.25, -30.25) * mm, "radius": 5 * mm, "construction": true});
            skCircle(sketch, "E511", {"center": v(-30.25, -30.25) * mm, "radius": 5 * mm, "construction": true});
            skLineSegment(sketch, "E512", {"start": v(-26.19, 26.2) * mm, "end": v(-30.25, 30.25) * mm, "construction": true});
            skLineSegment(sketch, "E513", {"start": v(-26.71, 26.71) * mm, "end": v(-33.79, 33.79) * mm, "construction": true});
            skLineSegment(sketch, "E514", {"start": v(-31.46, 31.46) * mm, "end": v(-28.13, 34.78) * mm, "construction": true});
            skLineSegment(sketch, "E515", {"start": v(-31.46, 31.46) * mm, "end": v(-34.78, 28.13) * mm, "construction": true});
            skLineSegment(sketch, "E516", {"start": v(26.2, 26.2) * mm, "end": v(30.25, 30.25) * mm, "construction": true});
            skLineSegment(sketch, "E517", {"start": v(26.71, 26.71) * mm, "end": v(33.79, 33.79) * mm, "construction": true});
            skLineSegment(sketch, "E518", {"start": v(31.46, 31.46) * mm, "end": v(34.78, 28.13) * mm, "construction": true});
            skLineSegment(sketch, "E519", {"start": v(31.46, 31.46) * mm, "end": v(28.13, 34.78) * mm, "construction": true});
            skLineSegment(sketch, "E520", {"start": v(26.19, -26.19) * mm, "end": v(30.25, -30.25) * mm, "construction": true});
            skLineSegment(sketch, "E521", {"start": v(26.71, -26.71) * mm, "end": v(33.79, -33.79) * mm, "construction": true});
            skLineSegment(sketch, "E522", {"start": v(31.46, -31.46) * mm, "end": v(34.78, -28.13) * mm, "construction": true});
            skLineSegment(sketch, "E523", {"start": v(31.46, -31.46) * mm, "end": v(28.13, -34.78) * mm, "construction": true});
            skLineSegment(sketch, "E524", {"start": v(-26.2, -26.2) * mm, "end": v(-30.25, -30.25) * mm, "construction": true});
            skLineSegment(sketch, "E525", {"start": v(-26.71, -26.71) * mm, "end": v(-33.79, -33.79) * mm, "construction": true});
            skLineSegment(sketch, "E526", {"start": v(-31.46, -31.46) * mm, "end": v(-28.13, -34.78) * mm, "construction": true});
            skLineSegment(sketch, "E527", {"start": v(-31.46, -31.46) * mm, "end": v(-34.78, -28.13) * mm, "construction": true});
            skArc(sketch, "E528", {"start": v(-28.13, 34.78) * mm, "mid": v(-33.79, 33.79) * mm, "end": v(-34.78, 28.13) * mm});
            skArc(sketch, "E529", {"start": v(34.78, 28.13) * mm, "mid": v(33.79, 33.79) * mm, "end": v(28.13, 34.78) * mm});
            skArc(sketch, "E530", {"start": v(28.13, -34.78) * mm, "mid": v(33.79, -33.79) * mm, "end": v(34.78, -28.13) * mm});
            skArc(sketch, "E531", {"start": v(-34.78, -28.13) * mm, "mid": v(-33.79, -33.79) * mm, "end": v(-28.13, -34.78) * mm});
            skLineSegment(sketch, "E532.bottom", {"start": v(24.5, -24.5) * mm, "end": v(-24.5, -24.5) * mm, "construction": true});
            skLineSegment(sketch, "E532.top", {"start": v(24.5, 24.5) * mm, "end": v(-24.5, 24.5) * mm, "construction": true});
            skLineSegment(sketch, "E532.left", {"start": v(24.5, -24.5) * mm, "end": v(24.5, 24.5) * mm, "construction": true});
            skLineSegment(sketch, "E532.right", {"start": v(-24.5, -24.5) * mm, "end": v(-24.5, 24.5) * mm, "construction": true});
            skLineSegment(sketch, "E533", {"start": v(34.78, 28.13) * mm, "end": v(28.26, 10.3) * mm});
            skLineSegment(sketch, "E534", {"start": v(28.26, -10.3) * mm, "end": v(34.78, -28.13) * mm});
            skLineSegment(sketch, "E535", {"start": v(-34.78, -28.13) * mm, "end": v(-28.26, -10.3) * mm});
            skLineSegment(sketch, "E536", {"start": v(-28.26, 10.3) * mm, "end": v(-34.78, 28.13) * mm});
            skPoint(sketch, "E537.visualSharp", {"position": v(24.5, 0) * mm});
            skArc(sketch, "E537.filletArc", {"start": v(28.26, 10.3) * mm, "mid": v(26.44, 0) * mm, "end": v(28.26, -10.3) * mm});
            skPoint(sketch, "E538.visualSharp", {"position": v(-24.5, 0) * mm});
            skArc(sketch, "E538.filletArc", {"start": v(-28.26, -10.3) * mm, "mid": v(-26.44, 0) * mm, "end": v(-28.26, 10.3) * mm});
            skPoint(sketch, "E539.visualSharp", {"position": v(0, -24.5) * mm});
            skLineSegment(sketch, "E540", {"start": v(-28.13, 34.78) * mm, "end": v(-11.4, 23.17) * mm});
            skLineSegment(sketch, "E541", {"start": v(11.4, 23.17) * mm, "end": v(28.13, 34.78) * mm});
            skPoint(sketch, "E542.visualSharp", {"position": v(0, 15.25) * mm});
            skArc(sketch, "E542.filletArc", {"start": v(-11.4, 23.17) * mm, "mid": v(0, 19.6) * mm, "end": v(11.4, 23.17) * mm});
            skCircle(sketch, "E543", {"center": v(-30.25, 30.25) * mm, "radius": 1.5 * mm});
            skCircle(sketch, "E544", {"center": v(-15.25, 15.25) * mm, "radius": 1.5 * mm});
            skCircle(sketch, "E545", {"center": v(15.25, 15.25) * mm, "radius": 1.5 * mm});
            skCircle(sketch, "E546", {"center": v(30.25, 30.25) * mm, "radius": 1.5 * mm});
            skCircle(sketch, "E547", {"center": v(30.25, -30.25) * mm, "radius": 1.5 * mm});
            skCircle(sketch, "E548", {"center": v(15.25, -15.25) * mm, "radius": 1.5 * mm});
            skCircle(sketch, "E549", {"center": v(-15.25, -15.25) * mm, "radius": 1.5 * mm});
            skCircle(sketch, "E550", {"center": v(-30.25, -30.25) * mm, "radius": 1.5 * mm});
            skLineSegment(sketch, "E551", {"start": v(-28.13, -34.78) * mm, "end": v(-11.4, -23.17) * mm});
            skLineSegment(sketch, "E552", {"start": v(11.4, -23.17) * mm, "end": v(28.13, -34.78) * mm});
            skPoint(sketch, "E553.visualSharp", {"position": v(0, -15.25) * mm});
            skArc(sketch, "E553.filletArc", {"start": v(11.4, -23.17) * mm, "mid": v(0, -19.6) * mm, "end": v(-11.4, -23.17) * mm});
            skSolve(sketch);
        }
        {
            var Q0;
            Q0=qSketchRegion(id+"F1",true);
            extrude(context, id + "F4", {"entities" : qUnion([Q0]), "operationType" : NewBodyOperationType.ADD, "depth" : 13 * mm, "hasSecondDirection" : true, "secondDirectionOppositeDirection" : false, "secondDirectionDepth" : 9 * mm});
        }
        {
            var Q0;
            Q0=qCreatedBy(makeId("Top.planeOp"),FACE);
            var sketch = newSketch(context, id + "F5", { "sketchPlane" : qUnion([Q0])});
            skLineSegment(sketch, "E554.bottom", {"start": v(-15.28, 17.52) * mm, "end": v(15.22, 17.52) * mm, "construction": true});
            skLineSegment(sketch, "E554.top", {"start": v(-15.25, -12.98) * mm, "end": v(15.25, -12.98) * mm, "construction": true});
            skLineSegment(sketch, "E554.left", {"start": v(-15.25, 17.52) * mm, "end": v(-15.25, -12.98) * mm, "construction": true});
            skLineSegment(sketch, "E554.right", {"start": v(15.22, 17.52) * mm, "end": v(15.22, -12.98) * mm, "construction": true});
            skPoint(sketch, "E554.middle", {"position": v(-0.01, 2.27) * mm});
            skLineSegment(sketch, "E555.bottom", {"start": v(30.24, 32.52) * mm, "end": v(-30.26, 32.52) * mm, "construction": true});
            skLineSegment(sketch, "E555.top", {"start": v(30.24, -27.98) * mm, "end": v(-30.26, -27.98) * mm, "construction": true});
            skLineSegment(sketch, "E555.left", {"start": v(30.24, 32.52) * mm, "end": v(30.24, -27.98) * mm, "construction": true});
            skLineSegment(sketch, "E555.right", {"start": v(-30.26, 32.52) * mm, "end": v(-30.26, -27.98) * mm, "construction": true});
            skLineSegment(sketch, "E556.bottom", {"start": v(-70.97, 73.23) * mm, "end": v(70.95, 73.23) * mm, "construction": true});
            skLineSegment(sketch, "E556.top", {"start": v(-70.97, -68.69) * mm, "end": v(70.95, -68.69) * mm, "construction": true});
            skLineSegment(sketch, "E556.left", {"start": v(-70.97, 73.23) * mm, "end": v(-70.97, -68.69) * mm, "construction": true});
            skLineSegment(sketch, "E556.right", {"start": v(70.95, 73.23) * mm, "end": v(70.95, -68.69) * mm, "construction": true});
            skCircle(sketch, "E557", {"center": v(70.95, 73.23) * mm, "radius": 8 * mm, "construction": true});
            skCircle(sketch, "E558", {"center": v(70.95, -68.69) * mm, "radius": 8 * mm, "construction": true});
            skCircle(sketch, "E559", {"center": v(-70.97, -68.69) * mm, "radius": 8 * mm, "construction": true});
            skCircle(sketch, "E560", {"center": v(-70.97, 73.23) * mm, "radius": 8 * mm, "construction": true});
            skCircle(sketch, "E561", {"center": v(70.95, 73.23) * mm, "radius": 9.5 * mm, "construction": true});
            skCircle(sketch, "E562", {"center": v(70.95, -68.69) * mm, "radius": 9.5 * mm, "construction": true});
            skCircle(sketch, "E563", {"center": v(-70.97, -68.69) * mm, "radius": 9.5 * mm, "construction": true});
            skCircle(sketch, "E564", {"center": v(-70.97, 73.23) * mm, "radius": 9.5 * mm, "construction": true});
            skCircle(sketch, "E565", {"center": v(70.95, 73.23) * mm, "radius": 14 * mm, "construction": true});
            skCircle(sketch, "E566", {"center": v(-70.97, 73.23) * mm, "radius": 14 * mm, "construction": true});
            skCircle(sketch, "E567", {"center": v(70.95, -68.69) * mm, "radius": 14 * mm, "construction": true});
            skCircle(sketch, "E568", {"center": v(-70.97, -68.69) * mm, "radius": 14 * mm, "construction": true});
            skCircle(sketch, "E569", {"center": v(70.95, 73.23) * mm, "radius": 63.5 * mm, "construction": true});
            skCircle(sketch, "E570", {"center": v(70.95, -68.69) * mm, "radius": 63.5 * mm, "construction": true});
            skCircle(sketch, "E571", {"center": v(-70.97, -68.69) * mm, "radius": 63.5 * mm, "construction": true});
            skCircle(sketch, "E572", {"center": v(-70.97, 73.23) * mm, "radius": 63.5 * mm, "construction": true});
            skLineSegment(sketch, "E573", {"start": v(-0.01, 32.52) * mm, "end": v(-0.01, 40.03) * mm, "construction": true});
            skLineSegment(sketch, "E574", {"start": v(-0.01, -27.98) * mm, "end": v(-0.01, -35.48) * mm, "construction": true});
            skLineSegment(sketch, "E575.bottom", {"start": v(-26.18, 28.53) * mm, "end": v(26.2, 28.53) * mm, "construction": true});
            skLineSegment(sketch, "E575.top", {"start": v(-26.22, -23.98) * mm, "end": v(26.16, -23.98) * mm, "construction": true});
            skLineSegment(sketch, "E575.left", {"start": v(-26.18, 28.53) * mm, "end": v(-26.18, -23.85) * mm, "construction": true});
            skLineSegment(sketch, "E575.right", {"start": v(26.2, 28.53) * mm, "end": v(26.2, -23.92) * mm, "construction": true});
            skCircle(sketch, "E576", {"center": v(30.24, 32.52) * mm, "radius": 5 * mm, "construction": true});
            skCircle(sketch, "E577", {"center": v(-30.26, 32.52) * mm, "radius": 5 * mm, "construction": true});
            skCircle(sketch, "E578", {"center": v(30.24, -27.98) * mm, "radius": 5 * mm, "construction": true});
            skCircle(sketch, "E579", {"center": v(-30.26, -27.98) * mm, "radius": 5 * mm, "construction": true});
            skLineSegment(sketch, "E580.bottom", {"start": v(24.49, 26.77) * mm, "end": v(-24.51, 26.77) * mm, "construction": true});
            skLineSegment(sketch, "E580.top", {"start": v(24.49, -22.23) * mm, "end": v(-24.51, -22.23) * mm, "construction": true});
            skLineSegment(sketch, "E580.left", {"start": v(24.49, 26.77) * mm, "end": v(24.49, -22.23) * mm, "construction": true});
            skLineSegment(sketch, "E580.right", {"start": v(-24.51, 26.77) * mm, "end": v(-24.51, -22.23) * mm, "construction": true});
            skLineSegment(sketch, "E581", {"start": v(-26.18, 28.53) * mm, "end": v(-30.26, 32.52) * mm, "construction": true});
            skLineSegment(sketch, "E582", {"start": v(-26.7, 29.02) * mm, "end": v(-33.83, 36.02) * mm, "construction": true});
            skLineSegment(sketch, "E583", {"start": v(-31.82, 34.05) * mm, "end": v(-28.67, 37.26) * mm, "construction": true});
            skLineSegment(sketch, "E584", {"start": v(-31.82, 34.05) * mm, "end": v(-34.97, 30.83) * mm, "construction": true});
            skArc(sketch, "E585", {"start": v(-28.67, 37.26) * mm, "mid": v(-33.83, 36.02) * mm, "end": v(-34.97, 30.83) * mm});
            skLineSegment(sketch, "E586", {"start": v(26.2, 28.53) * mm, "end": v(30.24, 32.52) * mm, "construction": true});
            skLineSegment(sketch, "E587", {"start": v(26.68, 29) * mm, "end": v(33.8, 36.04) * mm, "construction": true});
            skLineSegment(sketch, "E588", {"start": v(31.79, 34.06) * mm, "end": v(34.95, 30.86) * mm, "construction": true});
            skLineSegment(sketch, "E589", {"start": v(31.79, 34.06) * mm, "end": v(28.62, 37.26) * mm, "construction": true});
            skArc(sketch, "E590", {"start": v(34.95, 30.86) * mm, "mid": v(33.8, 36.04) * mm, "end": v(28.62, 37.26) * mm});
            skLineSegment(sketch, "E591", {"start": v(26.16, -23.98) * mm, "end": v(30.24, -27.98) * mm, "construction": true});
            skLineSegment(sketch, "E592", {"start": v(26.67, -24.48) * mm, "end": v(33.8, -31.48) * mm, "construction": true});
            skLineSegment(sketch, "E593", {"start": v(31.8, -29.5) * mm, "end": v(34.94, -26.29) * mm, "construction": true});
            skLineSegment(sketch, "E594", {"start": v(31.8, -29.5) * mm, "end": v(28.64, -32.72) * mm, "construction": true});
            skArc(sketch, "E595", {"start": v(28.64, -32.72) * mm, "mid": v(33.8, -31.48) * mm, "end": v(34.94, -26.29) * mm});
            skLineSegment(sketch, "E596", {"start": v(-26.22, -23.98) * mm, "end": v(-30.26, -27.98) * mm, "construction": true});
            skLineSegment(sketch, "E597", {"start": v(-26.7, -24.46) * mm, "end": v(-33.82, -31.5) * mm, "construction": true});
            skLineSegment(sketch, "E598", {"start": v(-31.81, -29.5) * mm, "end": v(-28.65, -32.7) * mm, "construction": true});
            skLineSegment(sketch, "E599", {"start": v(-31.81, -29.5) * mm, "end": v(-34.98, -26.31) * mm, "construction": true});
            skArc(sketch, "E600", {"start": v(-34.98, -26.31) * mm, "mid": v(-33.82, -31.5) * mm, "end": v(-28.65, -32.7) * mm});
            skLineSegment(sketch, "E601", {"start": v(-34.98, -26.31) * mm, "end": v(-28.29, -8.04) * mm});
            skLineSegment(sketch, "E602", {"start": v(-28.29, 12.59) * mm, "end": v(-34.97, 30.83) * mm});
            skLineSegment(sketch, "E603", {"start": v(34.95, 30.86) * mm, "end": v(28.26, 12.59) * mm});
            skLineSegment(sketch, "E604", {"start": v(28.26, -8.04) * mm, "end": v(34.94, -26.29) * mm});
            skPoint(sketch, "E605.visualSharp", {"position": v(24.49, 2.27) * mm});
            skArc(sketch, "E605.filletArc", {"start": v(28.26, 12.59) * mm, "mid": v(26.43, 2.27) * mm, "end": v(28.26, -8.04) * mm});
            skPoint(sketch, "E606.visualSharp", {"position": v(-24.51, 2.27) * mm});
            skArc(sketch, "E606.filletArc", {"start": v(-28.29, -8.04) * mm, "mid": v(-26.46, 2.27) * mm, "end": v(-28.29, 12.59) * mm});
            skLineSegment(sketch, "E607", {"start": v(-15.28, 22) * mm, "end": v(15.22, 22) * mm, "construction": true});
            skPoint(sketch, "E608.endSnap0", {"position": v(0, -12.98) * mm});
            skLineSegment(sketch, "E609", {"start": v(-15.25, -17.43) * mm, "end": v(15.25, -17.43) * mm, "construction": true});
            skLineSegment(sketch, "E610", {"start": v(-14.34, -35.48) * mm, "end": v(14.32, -35.48) * mm, "construction": true});
            skCircle(sketch, "E611", {"center": v(-30.26, 32.52) * mm, "radius": 1.5 * mm});
            skCircle(sketch, "E612", {"center": v(30.24, 32.52) * mm, "radius": 1.5 * mm});
            skCircle(sketch, "E613", {"center": v(15.22, 17.52) * mm, "radius": 1.5 * mm});
            skCircle(sketch, "E614", {"center": v(-15.28, 17.52) * mm, "radius": 1.5 * mm});
            skCircle(sketch, "E615", {"center": v(-15.25, -12.98) * mm, "radius": 1.5 * mm});
            skCircle(sketch, "E616", {"center": v(15.25, -12.98) * mm, "radius": 1.5 * mm});
            skCircle(sketch, "E617", {"center": v(30.24, -27.98) * mm, "radius": 1.5 * mm});
            skCircle(sketch, "E618", {"center": v(-30.26, -27.98) * mm, "radius": 1.5 * mm});
            skLineSegment(sketch, "E619", {"start": v(14.32, 40.03) * mm, "end": v(10.32, 40.03) * mm, "construction": true});
            skLineSegment(sketch, "E620", {"start": v(-14.34, 40.03) * mm, "end": v(-10.34, 40.03) * mm, "construction": true});
            skLineSegment(sketch, "E621", {"start": v(10.32, 40.03) * mm, "end": v(10.32, 36.03) * mm, "construction": true});
            skLineSegment(sketch, "E622", {"start": v(-10.34, 40.03) * mm, "end": v(-10.34, 36.03) * mm, "construction": true});
            skLineSegment(sketch, "E623", {"start": v(-0.01, 40.03) * mm, "end": v(-0.03, 17.52) * mm, "construction": true});
            skPoint(sketch, "E624.visualSharp", {"position": v(-14.34, -35.48) * mm});
            skPoint(sketch, "E625.visualSharp", {"position": v(14.32, -35.48) * mm});
            skCircle(sketch, "E626", {"center": v(-0.01, 2.27) * mm, "radius": 17.1 * mm, "construction": true});
            skLineSegment(sketch, "E627", {"start": v(-0.01, 2.27) * mm, "end": v(14.08, 16.37) * mm, "construction": true});
            skLineSegment(sketch, "E628", {"start": v(-0.01, 2.27) * mm, "end": v(-15.28, 17.52) * mm, "construction": true});
            skLineSegment(sketch, "E629", {"start": v(-0.01, 2.27) * mm, "end": v(-15.32, -13.05) * mm, "construction": true});
            skLineSegment(sketch, "E630", {"start": v(-0.01, 2.27) * mm, "end": v(15.25, -12.98) * mm, "construction": true});
            skLineSegment(sketch, "E631", {"start": v(-10.71, 12.96) * mm, "end": v(-7.89, 15.8) * mm, "construction": true});
            skLineSegment(sketch, "E632", {"start": v(-10.71, 12.96) * mm, "end": v(-13.54, 10.13) * mm, "construction": true});
            skLineSegment(sketch, "E633", {"start": v(9.01, 11.3) * mm, "end": v(11.84, 8.47) * mm, "construction": true});
            skLineSegment(sketch, "E634", {"start": v(9.01, 11.3) * mm, "end": v(6.19, 14.13) * mm, "construction": true});
            skLineSegment(sketch, "E635", {"start": v(9.8, -7.53) * mm, "end": v(12.63, -4.7) * mm, "construction": true});
            skLineSegment(sketch, "E636", {"start": v(9.8, -7.53) * mm, "end": v(6.97, -10.36) * mm, "construction": true});
            skLineSegment(sketch, "E637", {"start": v(-9.52, -7.25) * mm, "end": v(-6.7, -10.07) * mm, "construction": true});
            skLineSegment(sketch, "E638", {"start": v(-9.52, -7.25) * mm, "end": v(-12.35, -4.42) * mm, "construction": true});
            skLineSegment(sketch, "E639.bottom", {"start": v(6.34, 8.62) * mm, "end": v(-6.36, 8.62) * mm, "construction": true});
            skLineSegment(sketch, "E639.top", {"start": v(6.34, -4.08) * mm, "end": v(-6.36, -4.08) * mm, "construction": true});
            skLineSegment(sketch, "E639.left", {"start": v(6.34, 8.62) * mm, "end": v(6.34, -4.08) * mm, "construction": true});
            skLineSegment(sketch, "E639.right", {"start": v(-6.36, 8.62) * mm, "end": v(-6.36, -4.08) * mm, "construction": true});
            skLineSegment(sketch, "E640", {"start": v(6.19, 14.13) * mm, "end": v(8.92, 16.86) * mm, "construction": true});
            skLineSegment(sketch, "E641", {"start": v(11.84, 8.47) * mm, "end": v(14.57, 11.2) * mm, "construction": true});
            skLineSegment(sketch, "E642", {"start": v(7.98, 15.92) * mm, "end": v(1.4, 9.34) * mm});
            skLineSegment(sketch, "E643", {"start": v(-1.43, 9.34) * mm, "end": v(-8, 15.92) * mm});
            skLineSegment(sketch, "E644", {"start": v(-13.54, 10.13) * mm, "end": v(-14.6, 11.2) * mm, "construction": true});
            skLineSegment(sketch, "E645", {"start": v(-6.7, -10.07) * mm, "end": v(-8.93, -12.32) * mm, "construction": true});
            skLineSegment(sketch, "E646", {"start": v(-8, -11.38) * mm, "end": v(-1.43, -4.8) * mm});
            skLineSegment(sketch, "E647", {"start": v(1.4, -4.8) * mm, "end": v(7.98, -11.37) * mm});
            skLineSegment(sketch, "E648", {"start": v(13.64, 10.27) * mm, "end": v(7.06, 3.69) * mm});
            skLineSegment(sketch, "E649", {"start": v(7.06, 0.86) * mm, "end": v(13.64, -5.72) * mm});
            skPoint(sketch, "E650", {"position": v(-7.75, 17.52) * mm});
            skPoint(sketch, "E651", {"position": v(7.72, 17.52) * mm});
            skPoint(sketch, "E652", {"position": v(15.22, 10.04) * mm});
            skPoint(sketch, "E653", {"position": v(15.22, -5.5) * mm});
            skPoint(sketch, "E654", {"position": v(7.72, -12.98) * mm});
            skPoint(sketch, "E655", {"position": v(-7.75, -12.98) * mm});
            skPoint(sketch, "E656", {"position": v(-15.25, -5.5) * mm});
            skPoint(sketch, "E657", {"position": v(-15.25, 10.04) * mm});
            skLineSegment(sketch, "E658", {"start": v(-7.79, 17.5) * mm, "end": v(-7.75, 17.52) * mm});
            skLineSegment(sketch, "E659", {"start": v(7.76, 17.5) * mm, "end": v(7.72, 17.52) * mm});
            skLineSegment(sketch, "E660", {"start": v(15.22, 10.05) * mm, "end": v(15.22, 10.04) * mm});
            skLineSegment(sketch, "E661", {"start": v(15.22, -5.5) * mm, "end": v(15.22, -5.5) * mm});
            skLineSegment(sketch, "E662", {"start": v(7.76, -12.96) * mm, "end": v(7.72, -12.98) * mm});
            skLineSegment(sketch, "E663", {"start": v(-7.75, -12.98) * mm, "end": v(-7.78, -12.96) * mm});
            skLineSegment(sketch, "E664", {"start": v(-15.24, -5.5) * mm, "end": v(-15.25, -5.5) * mm});
            skLineSegment(sketch, "E665", {"start": v(-15.24, 10.05) * mm, "end": v(-15.25, 10.04) * mm});
            skPoint(sketch, "E666", {"position": v(-0.03, 19.37) * mm});
            skPoint(sketch, "E667", {"position": v(17.09, 2.27) * mm});
            skPoint(sketch, "E668", {"position": v(-17.11, 2.27) * mm});
            skPoint(sketch, "E669", {"position": v(-0.01, -14.83) * mm});
            skArc(sketch, "E670", {"start": v(15.22, -5.5) * mm, "mid": v(17.09, 2.27) * mm, "end": v(15.22, 10.04) * mm});
            skArc(sketch, "E671", {"start": v(-15.25, 10.04) * mm, "mid": v(-17.11, 2.27) * mm, "end": v(-15.25, -5.5) * mm});
            skPoint(sketch, "E672.visualSharp", {"position": v(-5.66, 2.27) * mm});
            skPoint(sketch, "E673.visualSharp", {"position": v(-14.6, 11.2) * mm});
            skArc(sketch, "E673.filletArc", {"start": v(-13.66, 10.27) * mm, "mid": v(-14.5, 10.55) * mm, "end": v(-15.24, 10.05) * mm});
            skPoint(sketch, "E674.visualSharp", {"position": v(-14.6, -6.66) * mm});
            skArc(sketch, "E674.filletArc", {"start": v(-15.24, -5.5) * mm, "mid": v(-14.5, -6.01) * mm, "end": v(-13.66, -5.73) * mm});
            skPoint(sketch, "E675.visualSharp", {"position": v(-8.94, 16.86) * mm});
            skArc(sketch, "E675.filletArc", {"start": v(-7.79, 17.5) * mm, "mid": v(-8.3, 16.77) * mm, "end": v(-8, 15.92) * mm});
            skPoint(sketch, "E676.visualSharp", {"position": v(8.92, 16.86) * mm});
            skArc(sketch, "E676.filletArc", {"start": v(7.98, 15.92) * mm, "mid": v(8.26, 16.77) * mm, "end": v(7.76, 17.5) * mm});
            skPoint(sketch, "E677.visualSharp", {"position": v(14.57, -6.66) * mm});
            skArc(sketch, "E677.filletArc", {"start": v(13.64, -5.72) * mm, "mid": v(14.48, -6) * mm, "end": v(15.22, -5.5) * mm});
            skPoint(sketch, "E678.visualSharp", {"position": v(14.57, 11.2) * mm});
            skArc(sketch, "E678.filletArc", {"start": v(15.22, 10.05) * mm, "mid": v(14.48, 10.55) * mm, "end": v(13.64, 10.27) * mm});
            skPoint(sketch, "E679.visualSharp", {"position": v(8.92, -12.3) * mm});
            skArc(sketch, "E679.filletArc", {"start": v(7.76, -12.96) * mm, "mid": v(8.27, -12.22) * mm, "end": v(7.98, -11.37) * mm});
            skPoint(sketch, "E680.visualSharp", {"position": v(-8.93, -12.32) * mm});
            skArc(sketch, "E680.filletArc", {"start": v(-8, -11.38) * mm, "mid": v(-8.28, -12.23) * mm, "end": v(-7.78, -12.96) * mm});
            skLineSegment(sketch, "E681", {"start": v(-13.66, 10.27) * mm, "end": v(-7.08, 3.68) * mm});
            skLineSegment(sketch, "E682", {"start": v(-13.66, -5.73) * mm, "end": v(-7.08, 0.86) * mm});
            skArc(sketch, "E683.filletArc", {"start": v(-7.08, 0.86) * mm, "mid": v(-6.5, 2.27) * mm, "end": v(-7.08, 3.68) * mm});
            skPoint(sketch, "E684.visualSharp", {"position": v(-0.01, -3.39) * mm});
            skArc(sketch, "E684.filletArc", {"start": v(1.4, -4.8) * mm, "mid": v(-0.01, -4.22) * mm, "end": v(-1.43, -4.8) * mm});
            skPoint(sketch, "E685.visualSharp", {"position": v(5.64, 2.27) * mm});
            skArc(sketch, "E685.filletArc", {"start": v(7.06, 3.69) * mm, "mid": v(6.47, 2.27) * mm, "end": v(7.06, 0.86) * mm});
            skPoint(sketch, "E686.visualSharp", {"position": v(-0.02, 7.93) * mm});
            skArc(sketch, "E686.filletArc", {"start": v(-1.43, 9.34) * mm, "mid": v(-0.02, 8.76) * mm, "end": v(1.4, 9.34) * mm});
            skLineSegment(sketch, "E687", {"start": v(-12.93, 15.17) * mm, "end": v(-11.16, 16.94) * mm, "construction": true});
            skLineSegment(sketch, "E688", {"start": v(-12.93, 15.17) * mm, "end": v(-14.7, 13.4) * mm, "construction": true});
            skLineSegment(sketch, "E689", {"start": v(-14.7, 13.4) * mm, "end": v(-27.43, 26.13) * mm, "construction": true});
            skPoint(sketch, "E690", {"position": v(-17.59, 16.3) * mm});
            skCircle(sketch, "E691", {"center": v(-15.28, 17.52) * mm, "radius": 4.62 * mm, "construction": true});
            skLineSegment(sketch, "E692", {"start": v(-27.43, 26.13) * mm, "end": v(-21.13, 10.9) * mm, "construction": true});
            skLineSegment(sketch, "E693", {"start": v(-15.28, 17.52) * mm, "end": v(-21.35, 11.45) * mm, "construction": true});
            skLineSegment(sketch, "E694", {"start": v(-18.88, 13.92) * mm, "end": v(-19.76, 13.03) * mm});
            skLineSegment(sketch, "E695", {"start": v(-22.2, 13.52) * mm, "end": v(-25.5, 21.5) * mm});
            skLineSegment(sketch, "E696", {"start": v(-23.88, 22.58) * mm, "end": v(-20.07, 18.78) * mm});
            skLineSegment(sketch, "E697", {"start": v(-19.86, 18.13) * mm, "end": v(-19.88, 18.01) * mm});
            skLineSegment(sketch, "E698", {"start": v(-18.86, 14.6) * mm, "end": v(-18.88, 14.62) * mm});
            skPoint(sketch, "E699", {"position": v(-19.7, 16.17) * mm});
            skArc(sketch, "E700", {"start": v(-19.88, 18.01) * mm, "mid": v(-19.72, 16.22) * mm, "end": v(-18.88, 14.62) * mm});
            skPoint(sketch, "E701.visualSharp", {"position": v(-27.43, 26.13) * mm});
            skArc(sketch, "E701.filletArc", {"start": v(-23.88, 22.58) * mm, "mid": v(-25.14, 22.7) * mm, "end": v(-25.5, 21.5) * mm});
            skPoint(sketch, "E702.visualSharp", {"position": v(-21.35, 11.45) * mm});
            skArc(sketch, "E702.filletArc", {"start": v(-22.2, 13.52) * mm, "mid": v(-21.12, 12.62) * mm, "end": v(-19.76, 13.03) * mm});
            skPoint(sketch, "E703.visualSharp", {"position": v(-18.55, 14.25) * mm});
            skArc(sketch, "E703.filletArc", {"start": v(-18.88, 13.92) * mm, "mid": v(-18.74, 14.26) * mm, "end": v(-18.86, 14.6) * mm});
            skPoint(sketch, "E704.visualSharp", {"position": v(-19.8, 18.5) * mm});
            skArc(sketch, "E704.filletArc", {"start": v(-19.86, 18.13) * mm, "mid": v(-19.89, 18.48) * mm, "end": v(-20.07, 18.78) * mm});
            skCircle(sketch, "E705", {"center": v(15.22, 17.54) * mm, "radius": 4.62 * mm, "construction": true});
            skLineSegment(sketch, "E706", {"start": v(15.22, 17.54) * mm, "end": v(12.89, 15.18) * mm, "construction": true});
            skLineSegment(sketch, "E707", {"start": v(12.89, 15.18) * mm, "end": v(14.67, 13.42) * mm, "construction": true});
            skLineSegment(sketch, "E708", {"start": v(12.89, 15.18) * mm, "end": v(11.1, 16.93) * mm, "construction": true});
            skLineSegment(sketch, "E709", {"start": v(11.1, 16.93) * mm, "end": v(23.84, 29.66) * mm, "construction": true});
            skLineSegment(sketch, "E710", {"start": v(14.67, 13.42) * mm, "end": v(27.3, 26.24) * mm, "construction": true});
            skLineSegment(sketch, "E711", {"start": v(15.22, 17.52) * mm, "end": v(21.34, 11.5) * mm, "construction": true});
            skLineSegment(sketch, "E712", {"start": v(21.34, 11.5) * mm, "end": v(27.3, 26.24) * mm, "construction": true});
            skLineSegment(sketch, "E713", {"start": v(19.8, 18.17) * mm, "end": v(19.81, 18.06) * mm});
            skLineSegment(sketch, "E714", {"start": v(18.82, 14.64) * mm, "end": v(18.84, 14.66) * mm});
            skLineSegment(sketch, "E715", {"start": v(20, 18.83) * mm, "end": v(23.79, 22.67) * mm});
            skLineSegment(sketch, "E716", {"start": v(25.43, 21.6) * mm, "end": v(22.18, 13.58) * mm});
            skLineSegment(sketch, "E717", {"start": v(19.74, 13.07) * mm, "end": v(18.84, 13.95) * mm});
            skPoint(sketch, "E718", {"position": v(19.64, 16.2) * mm});
            skArc(sketch, "E719", {"start": v(18.84, 14.66) * mm, "mid": v(19.66, 16.26) * mm, "end": v(19.81, 18.06) * mm});
            skPoint(sketch, "E720.visualSharp", {"position": v(18.5, 14.29) * mm});
            skArc(sketch, "E720.filletArc", {"start": v(18.82, 14.64) * mm, "mid": v(18.7, 14.3) * mm, "end": v(18.84, 13.95) * mm});
            skPoint(sketch, "E721.visualSharp", {"position": v(19.73, 18.55) * mm});
            skArc(sketch, "E721.filletArc", {"start": v(20, 18.83) * mm, "mid": v(19.82, 18.52) * mm, "end": v(19.8, 18.17) * mm});
            skPoint(sketch, "E722.visualSharp", {"position": v(27.3, 26.24) * mm});
            skArc(sketch, "E722.filletArc", {"start": v(25.43, 21.6) * mm, "mid": v(25.05, 22.8) * mm, "end": v(23.79, 22.67) * mm});
            skPoint(sketch, "E723.visualSharp", {"position": v(21.34, 11.5) * mm});
            skArc(sketch, "E723.filletArc", {"start": v(19.74, 13.07) * mm, "mid": v(21.1, 12.67) * mm, "end": v(22.18, 13.58) * mm});
            skCircle(sketch, "E724", {"center": v(-15.25, -12.98) * mm, "radius": 4.62 * mm, "construction": true});
            skCircle(sketch, "E725", {"center": v(15.25, -12.98) * mm, "radius": 4.62 * mm, "construction": true});
            skLineSegment(sketch, "E726", {"start": v(-15.25, -12.98) * mm, "end": v(-12.9, -10.63) * mm, "construction": true});
            skLineSegment(sketch, "E727", {"start": v(-12.9, -10.63) * mm, "end": v(-11.14, -12.4) * mm, "construction": true});
            skLineSegment(sketch, "E728", {"start": v(-12.9, -10.63) * mm, "end": v(-14.67, -8.87) * mm, "construction": true});
            skLineSegment(sketch, "E729", {"start": v(-11.14, -12.4) * mm, "end": v(-23.86, -25.13) * mm, "construction": true});
            skLineSegment(sketch, "E730", {"start": v(-14.67, -8.87) * mm, "end": v(-27.4, -21.6) * mm, "construction": true});
            skLineSegment(sketch, "E731", {"start": v(-15.25, -12.98) * mm, "end": v(-9.17, -19.05) * mm, "construction": true});
            skLineSegment(sketch, "E732", {"start": v(-15.25, -12.98) * mm, "end": v(-21.32, -6.9) * mm, "construction": true});
            skLineSegment(sketch, "E733", {"start": v(-25.48, -16.95) * mm, "end": v(-22.18, -8.98) * mm});
            skLineSegment(sketch, "E734", {"start": v(-19.73, -8.5) * mm, "end": v(-18.85, -9.37) * mm});
            skLineSegment(sketch, "E735", {"start": v(-23.85, -18.04) * mm, "end": v(-20.04, -14.23) * mm});
            skLineSegment(sketch, "E736", {"start": v(-18.83, -10.06) * mm, "end": v(-18.85, -10.08) * mm});
            skLineSegment(sketch, "E737", {"start": v(-19.83, -13.58) * mm, "end": v(-19.85, -13.47) * mm});
            skPoint(sketch, "E738", {"position": v(-19.68, -11.67) * mm});
            skArc(sketch, "E739", {"start": v(-18.85, -10.08) * mm, "mid": v(-19.68, -11.67) * mm, "end": v(-19.85, -13.47) * mm});
            skPoint(sketch, "E740.visualSharp", {"position": v(-18.52, -9.7) * mm});
            skArc(sketch, "E740.filletArc", {"start": v(-18.83, -10.06) * mm, "mid": v(-18.7, -9.71) * mm, "end": v(-18.85, -9.37) * mm});
            skPoint(sketch, "E741.visualSharp", {"position": v(-19.77, -13.96) * mm});
            skArc(sketch, "E741.filletArc", {"start": v(-20.04, -14.23) * mm, "mid": v(-19.85, -13.93) * mm, "end": v(-19.83, -13.58) * mm});
            skPoint(sketch, "E742.visualSharp", {"position": v(-27.4, -21.6) * mm});
            skArc(sketch, "E742.filletArc", {"start": v(-25.48, -16.95) * mm, "mid": v(-25.11, -18.17) * mm, "end": v(-23.85, -18.04) * mm});
            skPoint(sketch, "E743.visualSharp", {"position": v(-21.32, -6.9) * mm});
            skArc(sketch, "E743.filletArc", {"start": v(-19.73, -8.5) * mm, "mid": v(-21.09, -8.08) * mm, "end": v(-22.18, -8.98) * mm});
            skLineSegment(sketch, "E744", {"start": v(15.25, -12.98) * mm, "end": v(12.9, -10.63) * mm, "construction": true});
            skLineSegment(sketch, "E745", {"start": v(12.9, -10.63) * mm, "end": v(14.68, -8.87) * mm, "construction": true});
            skLineSegment(sketch, "E746", {"start": v(12.9, -10.63) * mm, "end": v(11.14, -12.4) * mm, "construction": true});
            skLineSegment(sketch, "E747", {"start": v(14.68, -8.87) * mm, "end": v(27.4, -21.59) * mm, "construction": true});
            skLineSegment(sketch, "E748", {"start": v(15.25, -12.98) * mm, "end": v(21.32, -6.9) * mm, "construction": true});
            skLineSegment(sketch, "E749", {"start": v(22.18, -8.97) * mm, "end": v(25.49, -16.95) * mm});
            skLineSegment(sketch, "E750", {"start": v(23.86, -18.04) * mm, "end": v(20.04, -14.23) * mm});
            skLineSegment(sketch, "E751", {"start": v(19.74, -8.49) * mm, "end": v(18.86, -9.37) * mm});
            skLineSegment(sketch, "E752", {"start": v(18.84, -10.06) * mm, "end": v(18.86, -10.08) * mm});
            skLineSegment(sketch, "E753", {"start": v(19.83, -13.58) * mm, "end": v(19.85, -13.46) * mm});
            skPoint(sketch, "E754", {"position": v(19.64, -11.53) * mm});
            skArc(sketch, "E755", {"start": v(19.85, -13.46) * mm, "mid": v(19.69, -11.67) * mm, "end": v(18.86, -10.08) * mm});
            skPoint(sketch, "E756.visualSharp", {"position": v(21.32, -6.9) * mm});
            skArc(sketch, "E756.filletArc", {"start": v(22.18, -8.97) * mm, "mid": v(21.1, -8.08) * mm, "end": v(19.74, -8.49) * mm});
            skPoint(sketch, "E757.visualSharp", {"position": v(19.77, -13.96) * mm});
            skArc(sketch, "E757.filletArc", {"start": v(19.83, -13.58) * mm, "mid": v(19.86, -13.93) * mm, "end": v(20.04, -14.23) * mm});
            skPoint(sketch, "E758.visualSharp", {"position": v(18.52, -9.7) * mm});
            skArc(sketch, "E758.filletArc", {"start": v(18.86, -9.37) * mm, "mid": v(18.71, -9.7) * mm, "end": v(18.84, -10.06) * mm});
            skPoint(sketch, "E759.visualSharp", {"position": v(27.4, -21.59) * mm});
            skArc(sketch, "E759.filletArc", {"start": v(23.86, -18.04) * mm, "mid": v(25.12, -18.16) * mm, "end": v(25.49, -16.95) * mm});
            skLineSegment(sketch, "E760", {"start": v(-0.01, -29.14) * mm, "end": v(15.24, -29.14) * mm, "construction": true});
            skPoint(sketch, "E761.visualSharp", {"position": v(-9.17, -19.05) * mm});
            skPoint(sketch, "E762.visualSharp", {"position": v(-11.98, -16.25) * mm});
            skPoint(sketch, "E763.visualSharp", {"position": v(-16.23, -17.5) * mm});
            skPoint(sketch, "E764.visualSharp", {"position": v(-23.86, -25.13) * mm});
            skLineSegment(sketch, "E765", {"start": v(15.25, -12.98) * mm, "end": v(9.18, -19.05) * mm, "construction": true});
            skLineSegment(sketch, "E766", {"start": v(11.14, -12.4) * mm, "end": v(23.88, -25.12) * mm, "construction": true});
            skPoint(sketch, "E767", {"position": v(13.76, -17.36) * mm});
            skPoint(sketch, "E768.visualSharp", {"position": v(9.18, -19.05) * mm});
            skPoint(sketch, "E769.visualSharp", {"position": v(11.98, -16.25) * mm});
            skPoint(sketch, "E770.visualSharp", {"position": v(23.88, -25.12) * mm});
            skPoint(sketch, "E771.visualSharp", {"position": v(16.24, -17.5) * mm});
            skPoint(sketch, "E772", {"position": v(-14.29, -17.5) * mm});
            skLineSegment(sketch, "E773", {"start": v(-28.67, 37.26) * mm, "end": v(-26.94, 36.26) * mm, "construction": true});
            skLineSegment(sketch, "E774", {"start": v(28.62, 37.26) * mm, "end": v(26.9, 36.24) * mm, "construction": true});
            skPoint(sketch, "E775", {"position": v(27.69, 36.82) * mm});
            skArc(sketch, "E776", {"start": v(28.62, 37.26) * mm, "mid": v(27.7, 36.84) * mm, "end": v(26.9, 36.24) * mm});
            skPoint(sketch, "E777", {"position": v(-27.73, 36.83) * mm});
            skArc(sketch, "E778", {"start": v(-26.94, 36.26) * mm, "mid": v(-27.76, 36.85) * mm, "end": v(-28.67, 37.26) * mm});
            skLineSegment(sketch, "E779", {"start": v(-26.94, 36.26) * mm, "end": v(-15.28, 26.77) * mm});
            skLineSegment(sketch, "E780", {"start": v(26.9, 36.24) * mm, "end": v(15.22, 26.77) * mm});
            skPoint(sketch, "E781", {"position": v(-0.03, 22) * mm});
            skFitSpline(sketch, "E782", {"points": [v(-15.28, 26.77) * mm, v(-0.03, 22) * mm, v(15.22, 26.77) * mm], "startDerivative": vector(26.4, -17.68) * mm, "endDerivative": vector(26.05, 17.77) * mm});
            skLineSegment(sketch, "E783", {"start": v(10.88, 23.81) * mm, "end": v(0, 23.82) * mm, "construction": true});
            skLineSegment(sketch, "E784", {"start": v(0, 23.82) * mm, "end": v(-10.88, 23.83) * mm, "construction": true});
            skLineSegment(sketch, "E785", {"start": v(-28.65, -32.7) * mm, "end": v(-26.92, -31.7) * mm, "construction": true});
            skLineSegment(sketch, "E786", {"start": v(28.64, -32.72) * mm, "end": v(26.91, -31.71) * mm, "construction": true});
            skPoint(sketch, "E787", {"position": v(27.67, -32.27) * mm});
            skArc(sketch, "E788", {"start": v(26.91, -31.71) * mm, "mid": v(27.73, -32.3) * mm, "end": v(28.64, -32.72) * mm});
            skPoint(sketch, "E789", {"position": v(-27.7, -32.27) * mm});
            skArc(sketch, "E790", {"start": v(-28.65, -32.7) * mm, "mid": v(-27.73, -32.29) * mm, "end": v(-26.92, -31.7) * mm});
            skLineSegment(sketch, "E791", {"start": v(-0.01, -29.14) * mm, "end": v(-15.26, -29.14) * mm, "construction": true});
            skLineSegment(sketch, "E792", {"start": v(-26.92, -31.7) * mm, "end": v(-15.26, -23.98) * mm});
            skLineSegment(sketch, "E793", {"start": v(26.91, -31.71) * mm, "end": v(15.24, -23.98) * mm});
            skLineSegment(sketch, "E794", {"start": v(-0.01, -14.83) * mm, "end": v(-0.01, -17.45) * mm, "construction": true});
            skLineSegment(sketch, "E795", {"start": v(-0.01, -17.45) * mm, "end": v(-0.01, -19.27) * mm, "construction": true});
            skFitSpline(sketch, "E796", {"points": [v(-15.26, -23.98) * mm, v(-0.01, -17.45) * mm, v(15.24, -23.98) * mm], "startDerivative": vector(30.5, 19.6) * mm, "endDerivative": vector(30.5, -19.6) * mm});
            skLineSegment(sketch, "E797", {"start": v(-0.01, -19.27) * mm, "end": v(10.87, -19.27) * mm, "construction": true});
            skLineSegment(sketch, "E798", {"start": v(-0.01, -19.27) * mm, "end": v(-10.9, -19.27) * mm, "construction": true});
            skLineSegment(sketch, "E799", {"start": v(0, -12.98) * mm, "end": v(0, -10.98) * mm, "construction": true});
            skFitSpline(sketch, "E800", {"points": [v(-7.75, -12.98) * mm, v(0, -10.98) * mm, v(7.72, -12.98) * mm], "startDerivative": vector(15.5, 6) * mm, "endDerivative": vector(15.45, -6) * mm});
            skLineSegment(sketch, "E801", {"start": v(-0.03, 17.52) * mm, "end": v(-0.03, 15.52) * mm, "construction": true});
            skFitSpline(sketch, "E802", {"points": [v(-7.75, 17.52) * mm, v(-0.03, 15.52) * mm, v(7.72, 17.52) * mm], "startDerivative": vector(15.45, -6) * mm, "endDerivative": vector(15.5, 6) * mm});
            skSolve(sketch);
        }
        {
            var Q0;
            Q0=qCreatedBy(makeId("Top.planeOp"),FACE);
            var sketch = newSketch(context, id + "F6", { "sketchPlane" : qUnion([Q0])});
            skLineSegment(sketch, "E803.bottom", {"start": v(-15.25, 15.28) * mm, "end": v(15.25, 15.28) * mm, "construction": true});
            skLineSegment(sketch, "E803.top", {"start": v(-15.25, -15.22) * mm, "end": v(15.25, -15.22) * mm, "construction": true});
            skLineSegment(sketch, "E803.left", {"start": v(-15.25, 15.28) * mm, "end": v(-15.25, -15.22) * mm, "construction": true});
            skLineSegment(sketch, "E803.right", {"start": v(15.25, 15.28) * mm, "end": v(15.25, -15.22) * mm, "construction": true});
            skPoint(sketch, "E803.middle", {"position": v(0, 0.03) * mm});
            skLineSegment(sketch, "E804.bottom", {"start": v(30.25, 30.28) * mm, "end": v(-30.25, 30.28) * mm, "construction": true});
            skLineSegment(sketch, "E804.top", {"start": v(30.25, -30.22) * mm, "end": v(-30.25, -30.22) * mm, "construction": true});
            skLineSegment(sketch, "E804.left", {"start": v(30.25, 30.28) * mm, "end": v(30.25, -30.22) * mm, "construction": true});
            skLineSegment(sketch, "E804.right", {"start": v(-30.25, 30.28) * mm, "end": v(-30.25, -30.22) * mm, "construction": true});
            skLineSegment(sketch, "E805.bottom", {"start": v(-74.25, 74.27) * mm, "end": v(74.25, 74.27) * mm, "construction": true});
            skLineSegment(sketch, "E805.top", {"start": v(-74.25, -74.22) * mm, "end": v(74.25, -74.22) * mm, "construction": true});
            skLineSegment(sketch, "E805.left", {"start": v(-74.25, 74.27) * mm, "end": v(-74.25, -74.22) * mm, "construction": true});
            skLineSegment(sketch, "E805.right", {"start": v(74.25, 74.27) * mm, "end": v(74.25, -74.22) * mm, "construction": true});
            skCircle(sketch, "E806", {"center": v(74.25, 74.27) * mm, "radius": 4.5 * mm, "construction": true});
            skCircle(sketch, "E807", {"center": v(-74.25, 74.27) * mm, "radius": 4.5 * mm, "construction": true});
            skCircle(sketch, "E808", {"center": v(74.25, -74.22) * mm, "radius": 4.5 * mm, "construction": true});
            skCircle(sketch, "E809", {"center": v(-74.25, -74.22) * mm, "radius": 4.5 * mm, "construction": true});
            skCircle(sketch, "E810", {"center": v(74.25, 74.27) * mm, "radius": 8 * mm, "construction": true});
            skCircle(sketch, "E811", {"center": v(74.25, -74.22) * mm, "radius": 8 * mm, "construction": true});
            skCircle(sketch, "E812", {"center": v(-74.25, -74.22) * mm, "radius": 8 * mm, "construction": true});
            skCircle(sketch, "E813", {"center": v(-74.25, 74.27) * mm, "radius": 8 * mm, "construction": true});
            skCircle(sketch, "E814", {"center": v(74.25, 74.27) * mm, "radius": 9.5 * mm, "construction": true});
            skCircle(sketch, "E815", {"center": v(74.25, -74.22) * mm, "radius": 9.5 * mm, "construction": true});
            skCircle(sketch, "E816", {"center": v(-74.25, -74.22) * mm, "radius": 9.5 * mm, "construction": true});
            skCircle(sketch, "E817", {"center": v(-74.25, 74.27) * mm, "radius": 9.5 * mm, "construction": true});
            skCircle(sketch, "E818", {"center": v(74.25, 74.27) * mm, "radius": 14 * mm, "construction": true});
            skCircle(sketch, "E819", {"center": v(-74.25, 74.27) * mm, "radius": 14 * mm, "construction": true});
            skCircle(sketch, "E820", {"center": v(74.25, -74.22) * mm, "radius": 14 * mm, "construction": true});
            skCircle(sketch, "E821", {"center": v(-74.25, -74.22) * mm, "radius": 14 * mm, "construction": true});
            skCircle(sketch, "E822", {"center": v(74.25, 74.27) * mm, "radius": 63.5 * mm, "construction": true});
            skCircle(sketch, "E823", {"center": v(74.25, -74.22) * mm, "radius": 63.5 * mm, "construction": true});
            skCircle(sketch, "E824", {"center": v(-74.25, -74.22) * mm, "radius": 63.5 * mm, "construction": true});
            skCircle(sketch, "E825", {"center": v(-74.25, 74.27) * mm, "radius": 63.5 * mm, "construction": true});
            skLineSegment(sketch, "E826", {"start": v(0, 30.28) * mm, "end": v(0, 33.77) * mm, "construction": true});
            skLineSegment(sketch, "E827", {"start": v(0, 33.77) * mm, "end": v(-15, 33.77) * mm, "construction": true});
            skLineSegment(sketch, "E828", {"start": v(0, 33.77) * mm, "end": v(15, 33.77) * mm, "construction": true});
            skLineSegment(sketch, "E829", {"start": v(0, -30.22) * mm, "end": v(0, -33.72) * mm, "construction": true});
            skLineSegment(sketch, "E830", {"start": v(0, -33.72) * mm, "end": v(-15, -33.72) * mm, "construction": true});
            skLineSegment(sketch, "E831", {"start": v(0, -33.72) * mm, "end": v(15, -33.72) * mm, "construction": true});
            skLineSegment(sketch, "E832.bottom", {"start": v(-26.19, 26.22) * mm, "end": v(26.2, 26.22) * mm, "construction": true});
            skLineSegment(sketch, "E832.top", {"start": v(-26.19, -26.16) * mm, "end": v(26.2, -26.16) * mm, "construction": true});
            skLineSegment(sketch, "E832.left", {"start": v(-26.19, 26.22) * mm, "end": v(-26.19, -26.16) * mm, "construction": true});
            skLineSegment(sketch, "E832.right", {"start": v(26.2, 26.22) * mm, "end": v(26.2, -26.16) * mm, "construction": true});
            skCircle(sketch, "E833", {"center": v(30.25, 30.28) * mm, "radius": 3.57 * mm, "construction": true});
            skCircle(sketch, "E834", {"center": v(-30.25, 30.28) * mm, "radius": 3.57 * mm, "construction": true});
            skCircle(sketch, "E835", {"center": v(30.25, -30.22) * mm, "radius": 3.57 * mm, "construction": true});
            skCircle(sketch, "E836", {"center": v(-30.25, -30.22) * mm, "radius": 3.57 * mm, "construction": true});
            skLineSegment(sketch, "E837", {"start": v(-74.25, 74.27) * mm, "end": v(74.25, -74.22) * mm, "construction": true});
            skLineSegment(sketch, "E838", {"start": v(0, -26.16) * mm, "end": v(17.54, -26.16) * mm, "construction": true});
            skLineSegment(sketch, "E839", {"start": v(0, -26.16) * mm, "end": v(-17.54, -26.16) * mm, "construction": true});
            skLineSegment(sketch, "E840", {"start": v(0, -33.72) * mm, "end": v(0, -44.57) * mm, "construction": true});
            skLineSegment(sketch, "E841", {"start": v(0, -44.57) * mm, "end": v(0, -48.1) * mm, "construction": true});
            skLineSegment(sketch, "E842", {"start": v(0, -44.57) * mm, "end": v(11, -44.57) * mm, "construction": true});
            skLineSegment(sketch, "E843", {"start": v(0, -44.57) * mm, "end": v(-11, -44.57) * mm, "construction": true});
            skLineSegment(sketch, "E844", {"start": v(-15.25, -15.22) * mm, "end": v(-19.25, -15.22) * mm, "construction": true});
            skLineSegment(sketch, "E845", {"start": v(15.25, -15.22) * mm, "end": v(19.25, -15.22) * mm, "construction": true});
            skLineSegment(sketch, "E846", {"start": v(15.25, 15.28) * mm, "end": v(19.25, 15.28) * mm, "construction": true});
            skLineSegment(sketch, "E847", {"start": v(-15.25, 15.28) * mm, "end": v(-19.25, 15.28) * mm, "construction": true});
            skLineSegment(sketch, "E848", {"start": v(-16.22, -31.94) * mm, "end": v(0, -31.94) * mm, "construction": true});
            skLineSegment(sketch, "E849", {"start": v(0, -31.94) * mm, "end": v(16.22, -31.94) * mm, "construction": true});
            skLineSegment(sketch, "E850", {"start": v(-12.6, -42.84) * mm, "end": v(0, -42.84) * mm, "construction": true});
            skLineSegment(sketch, "E851", {"start": v(0, -42.84) * mm, "end": v(12.6, -42.84) * mm, "construction": true});
            skFitSpline(sketch, "E852", {"points": [v(-11, -44.57) * mm, v(0, -48.1) * mm], "startDerivative": vector(9.3, -7.23) * mm, "endDerivative": vector(12, -2.3) * mm});
            skFitSpline(sketch, "E853", {"points": [v(11, -44.57) * mm, v(0, -48.1) * mm], "startDerivative": vector(-9.3, -7.23) * mm, "endDerivative": vector(-12, -2.3) * mm});
            skLineSegment(sketch, "E854", {"start": v(-7.9, -46.98) * mm, "end": v(0, -46.98) * mm, "construction": true});
            skLineSegment(sketch, "E855", {"start": v(0, -46.98) * mm, "end": v(7.9, -46.98) * mm, "construction": true});
            skLineSegment(sketch, "E856", {"start": v(-4, -47.35) * mm, "end": v(0, -47.35) * mm, "construction": true});
            skLineSegment(sketch, "E857", {"start": v(0, -47.35) * mm, "end": v(4, -47.35) * mm, "construction": true});
            skCircle(sketch, "E858", {"center": v(-8.33, -41.13) * mm, "radius": 1.5 * mm});
            skCircle(sketch, "E859", {"center": v(8.33, -41.13) * mm, "radius": 1.5 * mm});
            skFitSpline(sketch, "E860", {"points": [v(-15, 33.77) * mm, v(-19.25, 15.28) * mm], "startDerivative": vector(-1.66, -47.23) * mm, "endDerivative": vector(-4.95, -22.5) * mm});
            skFitSpline(sketch, "E861", {"points": [v(15, 33.77) * mm, v(19.25, 15.28) * mm], "startDerivative": vector(1.66, -47.23) * mm, "endDerivative": vector(4.95, -22.5) * mm});
            skLineSegment(sketch, "E862", {"start": v(-19.25, 15.28) * mm, "end": v(-19.25, -15.22) * mm});
            skLineSegment(sketch, "E863", {"start": v(19.25, 15.28) * mm, "end": v(19.25, -15.22) * mm});
            skLineSegment(sketch, "E864", {"start": v(15.55, 18.03) * mm, "end": v(0, 18.03) * mm, "construction": true});
            skLineSegment(sketch, "E865", {"start": v(0, 18.03) * mm, "end": v(-15.55, 18.03) * mm, "construction": true});
            skPoint(sketch, "E866.visualSharp", {"position": v(-17.54, -26.16) * mm});
            skPoint(sketch, "E867.visualSharp", {"position": v(17.54, -26.16) * mm});
            skFitSpline(sketch, "E868", {"points": [v(-19.25, -15.22) * mm, v(-17.54, -26.16) * mm, v(-12.6, -42.84) * mm, v(-11, -44.57) * mm], "startDerivative": vector(1.48, -36.7) * mm, "endDerivative": vector(10.67, -6.67) * mm});
            skFitSpline(sketch, "E869", {"points": [v(19.25, -15.22) * mm, v(17.54, -26.16) * mm, v(12.6, -42.84) * mm, v(11, -44.57) * mm], "startDerivative": vector(-1.5, -36.7) * mm, "endDerivative": vector(-10.67, -6.67) * mm});
            skLineSegment(sketch, "E870", {"start": v(-8.33, -41.13) * mm, "end": v(-13.33, -41.13) * mm, "construction": true});
            skLineSegment(sketch, "E871", {"start": v(-8.33, -41.13) * mm, "end": v(-8.33, -46.13) * mm, "construction": true});
            skLineSegment(sketch, "E872", {"start": v(8.33, -41.13) * mm, "end": v(13.33, -41.13) * mm, "construction": true});
            skLineSegment(sketch, "E873", {"start": v(8.33, -41.13) * mm, "end": v(8.33, -46.13) * mm, "construction": true});
            skCircle(sketch, "E874", {"center": v(-11.49, 43.94) * mm, "radius": 1.5 * mm});
            skCircle(sketch, "E875", {"center": v(11.5, 43.97) * mm, "radius": 1.5 * mm});
            skCircle(sketch, "E876", {"center": v(-15.25, 15.28) * mm, "radius": 1.5 * mm});
            skCircle(sketch, "E877", {"center": v(15.25, 15.28) * mm, "radius": 1.5 * mm});
            skCircle(sketch, "E878", {"center": v(15.25, -15.22) * mm, "radius": 1.5 * mm});
            skCircle(sketch, "E879", {"center": v(-15.25, -15.22) * mm, "radius": 1.5 * mm});
            skLineSegment(sketch, "E880.bottom", {"start": v(-13.67, 13.7) * mm, "end": v(13.68, 13.7) * mm, "construction": true});
            skLineSegment(sketch, "E880.top", {"start": v(-13.67, -13.65) * mm, "end": v(13.68, -13.65) * mm, "construction": true});
            skLineSegment(sketch, "E880.left", {"start": v(-13.68, 13.7) * mm, "end": v(-13.68, -13.65) * mm, "construction": true});
            skLineSegment(sketch, "E880.right", {"start": v(13.67, 13.7) * mm, "end": v(13.67, -13.65) * mm, "construction": true});
            skLineSegment(sketch, "E881.bottom", {"start": v(-4.75, 4.78) * mm, "end": v(4.75, 4.78) * mm, "construction": true});
            skLineSegment(sketch, "E881.top", {"start": v(-4.75, -4.72) * mm, "end": v(4.75, -4.72) * mm, "construction": true});
            skLineSegment(sketch, "E881.left", {"start": v(-4.75, 4.78) * mm, "end": v(-4.75, -4.72) * mm, "construction": true});
            skLineSegment(sketch, "E881.right", {"start": v(4.75, 4.78) * mm, "end": v(4.75, -4.72) * mm, "construction": true});
            skPoint(sketch, "E882", {"position": v(-4.75, 0.03) * mm});
            skPoint(sketch, "E883", {"position": v(0, 4.78) * mm});
            skPoint(sketch, "E884", {"position": v(4.75, 0.03) * mm});
            skPoint(sketch, "E885", {"position": v(0, -4.72) * mm});
            skLineSegment(sketch, "E886", {"start": v(-6.16, 1.44) * mm, "end": v(-11.97, 7.25) * mm});
            skLineSegment(sketch, "E887", {"start": v(-6.16, -1.39) * mm, "end": v(-11.97, -7.19) * mm});
            skLineSegment(sketch, "E888", {"start": v(-13.68, -6.48) * mm, "end": v(-13.68, 6.54) * mm});
            skLineSegment(sketch, "E889", {"start": v(6.16, -1.39) * mm, "end": v(11.97, -7.19) * mm});
            skLineSegment(sketch, "E890", {"start": v(6.16, 1.44) * mm, "end": v(11.97, 7.25) * mm});
            skLineSegment(sketch, "E891", {"start": v(13.67, 6.54) * mm, "end": v(13.67, -6.48) * mm});
            skArc(sketch, "E892.filletArc", {"start": v(-6.16, -1.39) * mm, "mid": v(-5.58, 0.03) * mm, "end": v(-6.16, 1.44) * mm});
            skPoint(sketch, "E893.visualSharp", {"position": v(-13.67, 8.95) * mm});
            skArc(sketch, "E893.filletArc", {"start": v(-11.97, 7.25) * mm, "mid": v(-13.06, 7.46) * mm, "end": v(-13.67, 6.54) * mm});
            skPoint(sketch, "E894.visualSharp", {"position": v(-13.67, -8.9) * mm});
            skArc(sketch, "E894.filletArc", {"start": v(-13.67, -6.48) * mm, "mid": v(-13.06, -7.4) * mm, "end": v(-11.97, -7.19) * mm});
            skArc(sketch, "E895.filletArc", {"start": v(6.16, 1.44) * mm, "mid": v(5.58, 0.03) * mm, "end": v(6.16, -1.39) * mm});
            skPoint(sketch, "E896.visualSharp", {"position": v(13.68, 8.95) * mm});
            skArc(sketch, "E896.filletArc", {"start": v(13.68, 6.54) * mm, "mid": v(13.06, 7.46) * mm, "end": v(11.97, 7.25) * mm});
            skPoint(sketch, "E897.visualSharp", {"position": v(13.68, -8.9) * mm});
            skArc(sketch, "E897.filletArc", {"start": v(11.97, -7.19) * mm, "mid": v(13.06, -7.4) * mm, "end": v(13.68, -6.48) * mm});
            skLineSegment(sketch, "E898", {"start": v(1.41, -6.14) * mm, "end": v(7.22, -11.94) * mm});
            skLineSegment(sketch, "E899", {"start": v(-1.41, -6.14) * mm, "end": v(-7.22, -11.94) * mm});
            skLineSegment(sketch, "E900", {"start": v(-6.51, -13.65) * mm, "end": v(6.51, -13.65) * mm});
            skArc(sketch, "E901.filletArc", {"start": v(1.41, -6.14) * mm, "mid": v(0, -5.55) * mm, "end": v(-1.41, -6.14) * mm});
            skPoint(sketch, "E902.visualSharp", {"position": v(8.92, -13.65) * mm});
            skArc(sketch, "E902.filletArc", {"start": v(6.51, -13.65) * mm, "mid": v(7.43, -13.03) * mm, "end": v(7.22, -11.94) * mm});
            skPoint(sketch, "E903.visualSharp", {"position": v(-8.93, -13.65) * mm});
            skArc(sketch, "E903.filletArc", {"start": v(-7.22, -11.94) * mm, "mid": v(-7.43, -13.03) * mm, "end": v(-6.51, -13.65) * mm});
            skLineSegment(sketch, "E904", {"start": v(0, -17.8) * mm, "end": v(13.36, -17.8) * mm, "construction": true});
            skPoint(sketch, "E905", {"position": v(0, -17.8) * mm});
            skLineSegment(sketch, "E906", {"start": v(0, -17.8) * mm, "end": v(-13.36, -17.8) * mm, "construction": true});
            skLineSegment(sketch, "E907", {"start": v(-8.92, -13.65) * mm, "end": v(-8.92, -17.8) * mm, "construction": true});
            skLineSegment(sketch, "E908", {"start": v(8.92, -13.65) * mm, "end": v(8.92, -17.8) * mm, "construction": true});
            skLineSegment(sketch, "E909", {"start": v(0, -17.8) * mm, "end": v(0, -26.72) * mm, "construction": true});
            skLineSegment(sketch, "E910", {"start": v(-7.22, -19.5) * mm, "end": v(-1.41, -25.3) * mm});
            skLineSegment(sketch, "E911", {"start": v(1.41, -25.3) * mm, "end": v(7.22, -19.5) * mm});
            skLineSegment(sketch, "E912", {"start": v(6.51, -17.8) * mm, "end": v(-6.51, -17.8) * mm});
            skPoint(sketch, "E913.visualSharp", {"position": v(-8.92, -17.8) * mm});
            skArc(sketch, "E913.filletArc", {"start": v(-6.51, -17.8) * mm, "mid": v(-7.43, -18.42) * mm, "end": v(-7.22, -19.5) * mm});
            skPoint(sketch, "E914.visualSharp", {"position": v(8.92, -17.8) * mm});
            skArc(sketch, "E914.filletArc", {"start": v(7.22, -19.5) * mm, "mid": v(7.43, -18.42) * mm, "end": v(6.51, -17.8) * mm});
            skPoint(sketch, "E915.visualSharp", {"position": v(0, -26.72) * mm});
            skArc(sketch, "E915.filletArc", {"start": v(-1.41, -25.3) * mm, "mid": v(0, -25.9) * mm, "end": v(1.41, -25.3) * mm});
            skLineSegment(sketch, "E916", {"start": v(0, -21.22) * mm, "end": v(-11.7, -21.22) * mm, "construction": true});
            skLineSegment(sketch, "E917", {"start": v(0, -21.22) * mm, "end": v(11.7, -21.22) * mm, "construction": true});
            skLineSegment(sketch, "E918", {"start": v(-10.43, -22.48) * mm, "end": v(-4.5, -28.4) * mm});
            skLineSegment(sketch, "E919", {"start": v(-3.92, -29.82) * mm, "end": v(-3.92, -33) * mm});
            skLineSegment(sketch, "E920", {"start": v(-11.27, -22.95) * mm, "end": v(-9.07, -31.94) * mm});
            skArc(sketch, "E921", {"start": v(-9.07, -31.94) * mm, "mid": v(-6.94, -34.19) * mm, "end": v(-3.92, -33.5) * mm, "construction": true});
            skLineSegment(sketch, "E922", {"start": v(-4.32, -33.8) * mm, "end": v(-4.4, -33.86) * mm});
            skPoint(sketch, "E923", {"position": v(-6.94, -34.19) * mm});
            skArc(sketch, "E924", {"start": v(-9.07, -31.94) * mm, "mid": v(-7.22, -34.09) * mm, "end": v(-4.4, -33.86) * mm});
            skPoint(sketch, "E925.visualSharp", {"position": v(-11.7, -21.22) * mm});
            skArc(sketch, "E925.filletArc", {"start": v(-10.43, -22.48) * mm, "mid": v(-11.03, -22.4) * mm, "end": v(-11.27, -22.95) * mm});
            skPoint(sketch, "E926.visualSharp", {"position": v(-3.92, -29) * mm});
            skArc(sketch, "E926.filletArc", {"start": v(-3.92, -29.82) * mm, "mid": v(-4.07, -29.06) * mm, "end": v(-4.5, -28.4) * mm});
            skPoint(sketch, "E927.visualSharp", {"position": v(-3.92, -33.5) * mm});
            skArc(sketch, "E927.filletArc", {"start": v(-4.32, -33.8) * mm, "mid": v(-4.03, -33.44) * mm, "end": v(-3.92, -33) * mm});
            skLineSegment(sketch, "E928", {"start": v(10.43, -22.48) * mm, "end": v(4.5, -28.4) * mm});
            skLineSegment(sketch, "E929", {"start": v(3.92, -29.82) * mm, "end": v(3.92, -33) * mm});
            skLineSegment(sketch, "E930", {"start": v(3.92, -31.94) * mm, "end": v(9.07, -31.94) * mm, "construction": true});
            skArc(sketch, "E931", {"start": v(3.92, -33.5) * mm, "mid": v(6.94, -34.19) * mm, "end": v(9.07, -31.94) * mm, "construction": true});
            skLineSegment(sketch, "E932", {"start": v(11.27, -22.95) * mm, "end": v(9.07, -31.94) * mm});
            skLineSegment(sketch, "E933", {"start": v(4.32, -33.8) * mm, "end": v(4.4, -33.86) * mm});
            skPoint(sketch, "E934", {"position": v(6.94, -34.19) * mm});
            skArc(sketch, "E935", {"start": v(4.4, -33.86) * mm, "mid": v(7.22, -34.09) * mm, "end": v(9.07, -31.94) * mm});
            skPoint(sketch, "E936.visualSharp", {"position": v(3.92, -29) * mm});
            skArc(sketch, "E936.filletArc", {"start": v(4.5, -28.4) * mm, "mid": v(4.07, -29.06) * mm, "end": v(3.92, -29.82) * mm});
            skPoint(sketch, "E937.visualSharp", {"position": v(3.92, -33.5) * mm});
            skArc(sketch, "E937.filletArc", {"start": v(3.92, -33) * mm, "mid": v(4.03, -33.44) * mm, "end": v(4.32, -33.8) * mm});
            skPoint(sketch, "E938.visualSharp", {"position": v(11.7, -21.22) * mm});
            skArc(sketch, "E938.filletArc", {"start": v(11.27, -22.95) * mm, "mid": v(11.03, -22.4) * mm, "end": v(10.43, -22.48) * mm});
            skLineSegment(sketch, "E939", {"start": v(-8.92, -13.65) * mm, "end": v(-8.92, 13.7) * mm, "construction": true});
            skLineSegment(sketch, "E940", {"start": v(8.92, -13.65) * mm, "end": v(8.92, 13.7) * mm, "construction": true});
            skLineSegment(sketch, "E941", {"start": v(-1.41, 6.2) * mm, "end": v(-7.22, 12) * mm});
            skLineSegment(sketch, "E942", {"start": v(1.41, 6.2) * mm, "end": v(7.22, 12) * mm});
            skLineSegment(sketch, "E943", {"start": v(6.51, 13.7) * mm, "end": v(-6.51, 13.7) * mm});
            skArc(sketch, "E944.filletArc", {"start": v(-1.41, 6.2) * mm, "mid": v(0, 5.6) * mm, "end": v(1.41, 6.2) * mm});
            skPoint(sketch, "E945.visualSharp", {"position": v(8.92, 13.7) * mm});
            skArc(sketch, "E945.filletArc", {"start": v(7.22, 12) * mm, "mid": v(7.43, 13.09) * mm, "end": v(6.51, 13.7) * mm});
            skPoint(sketch, "E946.visualSharp", {"position": v(-8.93, 13.7) * mm});
            skArc(sketch, "E946.filletArc", {"start": v(-6.51, 13.7) * mm, "mid": v(-7.43, 13.09) * mm, "end": v(-7.22, 12) * mm});
            skLineSegment(sketch, "E947", {"start": v(0, 32.03) * mm, "end": v(8.5, 32.03) * mm, "construction": true});
            skPoint(sketch, "E947.endSnap0", {"position": v(0, 32.03) * mm});
            skLineSegment(sketch, "E948", {"start": v(0, 32.03) * mm, "end": v(-8.5, 32.03) * mm, "construction": true});
            skPoint(sketch, "E949.visualSharp", {"position": v(-8.5, 24.54) * mm});
            skPoint(sketch, "E950.visualSharp", {"position": v(8.5, 24.54) * mm});
            skLineSegment(sketch, "E951", {"start": v(0, 33.77) * mm, "end": v(0, 47.71) * mm, "construction": true});
            skLineSegment(sketch, "E952", {"start": v(0, 47.71) * mm, "end": v(-15.08, 47.71) * mm, "construction": true});
            skLineSegment(sketch, "E953", {"start": v(0, 47.71) * mm, "end": v(15, 47.71) * mm, "construction": true});
            skLineSegment(sketch, "E954", {"start": v(-15.08, 31.86) * mm, "end": v(-15.08, 47.71) * mm});
            skLineSegment(sketch, "E955", {"start": v(15.08, 31.86) * mm, "end": v(15, 47.71) * mm});
            skLineSegment(sketch, "E956", {"start": v(0, 42.68) * mm, "end": v(-8.5, 42.68) * mm, "construction": true});
            skLineSegment(sketch, "E957", {"start": v(0, 42.68) * mm, "end": v(8.5, 42.68) * mm, "construction": true});
            skLineSegment(sketch, "E958", {"start": v(-15.08, 47.71) * mm, "end": v(-8.5, 47.71) * mm});
            skLineSegment(sketch, "E959", {"start": v(-8.5, 47.71) * mm, "end": v(-8.5, 37) * mm});
            skLineSegment(sketch, "E960", {"start": v(15, 47.71) * mm, "end": v(8.5, 47.71) * mm});
            skLineSegment(sketch, "E961", {"start": v(8.5, 47.71) * mm, "end": v(8.5, 37) * mm});
            skLineSegment(sketch, "E962", {"start": v(8.5, 37) * mm, "end": v(-8.5, 37) * mm});
            skSolve(sketch);
        }
        {
            var Q0;
            Q0=qSketchRegion(id+"F6",true);
            extrude(context, id + "F7", {"entities" : qUnion([Q0]), "depth" : 28.5 * mm, "hasSecondDirection" : true, "secondDirectionOppositeDirection" : false, "secondDirectionDepth" : 27 * mm});
        }
        {
            var Q0;
            Q0=qSketchRegion(id+"F5",true);
            extrude(context, id + "F8", {"entities" : qUnion([Q0]), "depth" : 15 * mm, "hasSecondDirection" : true, "secondDirectionOppositeDirection" : false, "secondDirectionDepth" : 13 * mm});
        }
    });
